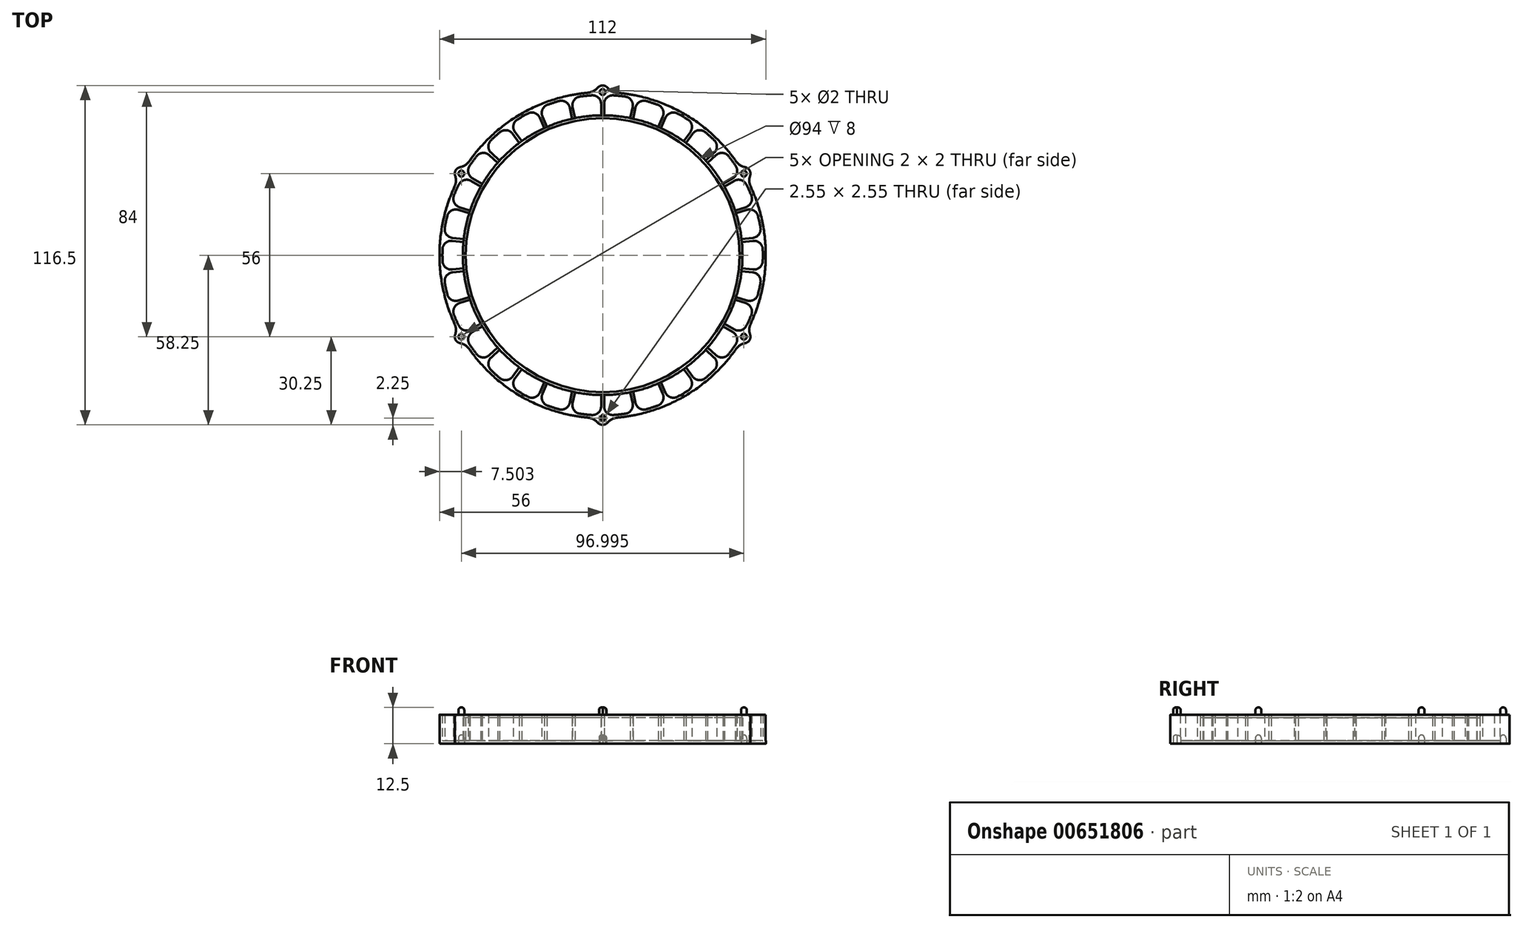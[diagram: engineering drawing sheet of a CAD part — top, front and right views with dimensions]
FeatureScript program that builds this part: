
annotation { "Feature Type Name" : "Feature", "Feature Type Description" : "" }
export const myFeature = defineFeature(function(context is Context, id is Id, definition is map)
    precondition{}
    {
        {
            var Q0;
            Q0=qCreatedBy(makeId("Top.planeOp"),FACE);
            var sketch = newSketch(context, id + "F0", { "sketchPlane" : qUnion([Q0])});
            skCircle(sketch, "E0", {"center": v(0, 0) * mm, "radius": 55 * mm});
            skCircle(sketch, "E1", {"center": v(0, 0) * mm, "radius": 56 * mm});
            skLineSegment(sketch, "E2", {"start": v(0, 60.2) * mm, "end": v(0, -62.26) * mm, "construction": true});
            skLineSegment(sketch, "E3", {"start": v(-62.84, 0) * mm, "end": v(64.36, 0) * mm, "construction": true});
            skLineSegment(sketch, "E4", {"start": v(55, 0) * mm, "end": v(56, 0) * mm});
            skCircle(sketch, "E5", {"center": v(0, 0) * mm, "radius": 48 * mm});
            skCircle(sketch, "E6", {"center": v(0, 0) * mm, "radius": 47 * mm});
            skLineSegment(sketch, "E7.left", {"start": v(-56, 0.5) * mm, "end": v(-56, -0.5) * mm});
            skLineSegment(sketch, "E7.right", {"start": v(56, 0.5) * mm, "end": v(56, -0.5) * mm});
            skLineSegment(sketch, "E8.bottom", {"start": v(0.5, -56) * mm, "end": v(-0.5, -56) * mm});
            skLineSegment(sketch, "E8.top", {"start": v(0.5, 56) * mm, "end": v(-0.5, 56) * mm});
            skLineSegment(sketch, "E8.left", {"start": v(0.5, -56) * mm, "end": v(0.5, 56) * mm});
            skLineSegment(sketch, "E8.right", {"start": v(-0.5, -56) * mm, "end": v(-0.5, 56) * mm});
            skLineSegment(sketch, "E9.bottom", {"start": v(12.13, 54.67) * mm, "end": v(-11.15, -54.88) * mm});
            skLineSegment(sketch, "E9.top", {"start": v(11.15, 54.88) * mm, "end": v(-12.13, -54.67) * mm});
            skLineSegment(sketch, "E9.left", {"start": v(12.13, 54.67) * mm, "end": v(11.15, 54.88) * mm});
            skLineSegment(sketch, "E9.right", {"start": v(-11.15, -54.88) * mm, "end": v(-12.13, -54.67) * mm});
            skLineSegment(sketch, "E10.bottom", {"start": v(-22.32, -51.36) * mm, "end": v(-23.23, -50.95) * mm});
            skLineSegment(sketch, "E10.top", {"start": v(23.23, 50.95) * mm, "end": v(22.32, 51.36) * mm});
            skLineSegment(sketch, "E10.left", {"start": v(-22.32, -51.36) * mm, "end": v(23.23, 50.95) * mm});
            skLineSegment(sketch, "E10.right", {"start": v(-23.23, -50.95) * mm, "end": v(22.32, 51.36) * mm});
            skLineSegment(sketch, "E11.bottom", {"start": v(32.51, 45.6) * mm, "end": v(33.32, 45) * mm});
            skLineSegment(sketch, "E11.top", {"start": v(-33.32, -45) * mm, "end": v(-32.51, -45.6) * mm});
            skLineSegment(sketch, "E11.left", {"start": v(32.51, 45.6) * mm, "end": v(-33.32, -45) * mm});
            skLineSegment(sketch, "E11.right", {"start": v(33.32, 45) * mm, "end": v(-32.51, -45.6) * mm});
            skLineSegment(sketch, "E12.bottom", {"start": v(-41.28, -37.84) * mm, "end": v(-41.95, -37.1) * mm});
            skLineSegment(sketch, "E12.top", {"start": v(41.95, 37.1) * mm, "end": v(41.28, 37.84) * mm});
            skLineSegment(sketch, "E12.left", {"start": v(-41.28, -37.84) * mm, "end": v(41.95, 37.1) * mm});
            skLineSegment(sketch, "E12.right", {"start": v(-41.95, -37.1) * mm, "end": v(41.28, 37.84) * mm});
            skLineSegment(sketch, "E13.bottom", {"start": v(48.25, 28.43) * mm, "end": v(48.75, 27.57) * mm});
            skLineSegment(sketch, "E13.top", {"start": v(-48.75, -27.57) * mm, "end": v(-48.25, -28.43) * mm});
            skLineSegment(sketch, "E13.left", {"start": v(48.25, 28.43) * mm, "end": v(-48.75, -27.57) * mm});
            skLineSegment(sketch, "E13.right", {"start": v(48.75, 27.57) * mm, "end": v(-48.25, -28.43) * mm});
            skLineSegment(sketch, "E14.bottom", {"start": v(-53.1, -17.78) * mm, "end": v(-53.41, -16.83) * mm});
            skLineSegment(sketch, "E14.top", {"start": v(53.41, 16.83) * mm, "end": v(53.1, 17.78) * mm});
            skLineSegment(sketch, "E14.left", {"start": v(-53.1, -17.78) * mm, "end": v(53.41, 16.83) * mm});
            skLineSegment(sketch, "E14.right", {"start": v(-53.41, -16.83) * mm, "end": v(53.1, 17.78) * mm});
            skLineSegment(sketch, "E15.bottom", {"start": v(55.64, 6.35) * mm, "end": v(55.74, 5.36) * mm});
            skLineSegment(sketch, "E15.top", {"start": v(-55.74, -5.36) * mm, "end": v(-55.64, -6.35) * mm});
            skLineSegment(sketch, "E15.left", {"start": v(55.64, 6.35) * mm, "end": v(-55.74, -5.36) * mm});
            skLineSegment(sketch, "E15.right", {"start": v(55.74, 5.36) * mm, "end": v(-55.64, -6.35) * mm});
            skLineSegment(sketch, "E16.bottom", {"start": v(-55.74, 5.36) * mm, "end": v(-55.64, 6.35) * mm});
            skLineSegment(sketch, "E16.top", {"start": v(55.64, -6.35) * mm, "end": v(55.74, -5.36) * mm});
            skLineSegment(sketch, "E16.left", {"start": v(-55.74, 5.36) * mm, "end": v(55.64, -6.35) * mm});
            skLineSegment(sketch, "E16.right", {"start": v(-55.64, 6.35) * mm, "end": v(55.74, -5.36) * mm});
            skLineSegment(sketch, "E17.bottom", {"start": v(53.41, -16.83) * mm, "end": v(53.1, -17.78) * mm});
            skLineSegment(sketch, "E17.top", {"start": v(-53.1, 17.78) * mm, "end": v(-53.41, 16.83) * mm});
            skLineSegment(sketch, "E17.left", {"start": v(53.41, -16.83) * mm, "end": v(-53.1, 17.78) * mm});
            skLineSegment(sketch, "E17.right", {"start": v(53.1, -17.78) * mm, "end": v(-53.41, 16.83) * mm});
            skLineSegment(sketch, "E18.bottom", {"start": v(48.75, -27.57) * mm, "end": v(48.25, -28.43) * mm});
            skLineSegment(sketch, "E18.top", {"start": v(-48.25, 28.43) * mm, "end": v(-48.75, 27.57) * mm});
            skLineSegment(sketch, "E18.left", {"start": v(48.75, -27.57) * mm, "end": v(-48.25, 28.43) * mm});
            skLineSegment(sketch, "E18.right", {"start": v(48.25, -28.43) * mm, "end": v(-48.75, 27.57) * mm});
            skLineSegment(sketch, "E19.bottom", {"start": v(-41.95, 37.1) * mm, "end": v(-41.28, 37.84) * mm});
            skLineSegment(sketch, "E19.top", {"start": v(41.28, -37.84) * mm, "end": v(41.95, -37.1) * mm});
            skLineSegment(sketch, "E19.left", {"start": v(-41.95, 37.1) * mm, "end": v(41.28, -37.84) * mm});
            skLineSegment(sketch, "E19.right", {"start": v(-41.28, 37.84) * mm, "end": v(41.95, -37.1) * mm});
            skLineSegment(sketch, "E20.bottom", {"start": v(-33.32, 45) * mm, "end": v(-32.51, 45.6) * mm});
            skLineSegment(sketch, "E20.top", {"start": v(32.51, -45.6) * mm, "end": v(33.32, -45) * mm});
            skLineSegment(sketch, "E20.left", {"start": v(-33.32, 45) * mm, "end": v(32.51, -45.6) * mm});
            skLineSegment(sketch, "E20.right", {"start": v(-32.51, 45.6) * mm, "end": v(33.32, -45) * mm});
            skLineSegment(sketch, "E21.bottom", {"start": v(-23.23, 50.95) * mm, "end": v(-22.32, 51.36) * mm});
            skLineSegment(sketch, "E21.top", {"start": v(22.32, -51.36) * mm, "end": v(23.23, -50.95) * mm});
            skLineSegment(sketch, "E21.left", {"start": v(-23.23, 50.95) * mm, "end": v(22.32, -51.36) * mm});
            skLineSegment(sketch, "E21.right", {"start": v(-22.32, 51.36) * mm, "end": v(23.23, -50.95) * mm});
            skLineSegment(sketch, "E22.bottom", {"start": v(-12.13, 54.67) * mm, "end": v(-11.15, 54.88) * mm});
            skLineSegment(sketch, "E22.top", {"start": v(11.15, -54.88) * mm, "end": v(12.13, -54.67) * mm});
            skLineSegment(sketch, "E22.left", {"start": v(-12.13, 54.67) * mm, "end": v(11.15, -54.88) * mm});
            skLineSegment(sketch, "E22.right", {"start": v(-11.15, 54.88) * mm, "end": v(12.13, -54.67) * mm});
            skSolve(sketch);
        }
        {
            var Q0;
            {var subQ0=sQuery(id+"F0.wireOp",EDGE,"E7.left");Q0=makeQuery(id+"F0.imprint","IMPRINT",FACE,{"disambiguationData":[TD([[makeQuery(id+"F0.imprint","IMPRINT",EDGE,{"derivedFrom":subQ0}),1.0]])]});}
            var Q1;
            {var subQ5=sQuery(id+"F0.wireOp",EDGE,"E8.top");Q1=makeQuery(id+"F0.imprint","IMPRINT",FACE,{"disambiguationData":[TD([[makeQuery(id+"F0.imprint","IMPRINT",EDGE,{"derivedFrom":subQ5}),1.0]])]});}
            var Q2;
            {var subQ0=sQuery(id+"F0.wireOp",EDGE,"E9.top");var subQ1=sQuery(id+"F0.wireOp",EDGE,"E0");var subQ2=makeQuery(id+"F0.imprint","INTERSECT",VERTEX,{"disambiguationData":[OD(0.0)],"derivedFrom":[subQ1,subQ0]});Q2=makeQuery(id+"F0.imprint","IMPRINT",FACE,{"disambiguationData":[TD([[makeQuery(id+"F0.imprint","IMPRINT",EDGE,{"disambiguationData":[TD([[subQ2,-1.0]])],"derivedFrom":subQ1}),-1.0]])]});}
            var Q3;
            {var subQ5=sQuery(id+"F0.wireOp",EDGE,"E9.left");Q3=makeQuery(id+"F0.imprint","IMPRINT",FACE,{"disambiguationData":[TD([[makeQuery(id+"F0.imprint","IMPRINT",EDGE,{"derivedFrom":subQ5}),1.0]])]});}
            var Q4;
            {var subQ0=sQuery(id+"F0.wireOp",EDGE,"E10.right");var subQ1=sQuery(id+"F0.wireOp",EDGE,"E0");var subQ2=makeQuery(id+"F0.imprint","INTERSECT",VERTEX,{"disambiguationData":[OD(0.0)],"derivedFrom":[subQ1,subQ0]});Q4=makeQuery(id+"F0.imprint","IMPRINT",FACE,{"disambiguationData":[TD([[makeQuery(id+"F0.imprint","IMPRINT",EDGE,{"disambiguationData":[TD([[subQ2,-1.0]])],"derivedFrom":subQ1}),-1.0]])]});}
            var Q5;
            {var subQ5=sQuery(id+"F0.wireOp",EDGE,"E10.top");Q5=makeQuery(id+"F0.imprint","IMPRINT",FACE,{"disambiguationData":[TD([[makeQuery(id+"F0.imprint","IMPRINT",EDGE,{"derivedFrom":subQ5}),1.0]])]});}
            var Q6;
            {var subQ0=sQuery(id+"F0.wireOp",EDGE,"E11.left");var subQ1=sQuery(id+"F0.wireOp",EDGE,"E0");var subQ2=makeQuery(id+"F0.imprint","INTERSECT",VERTEX,{"disambiguationData":[OD(0.0)],"derivedFrom":[subQ1,subQ0]});Q6=makeQuery(id+"F0.imprint","IMPRINT",FACE,{"disambiguationData":[TD([[makeQuery(id+"F0.imprint","IMPRINT",EDGE,{"disambiguationData":[TD([[subQ2,-1.0]])],"derivedFrom":subQ1}),-1.0]])]});}
            var Q7;
            {var subQ3=sQuery(id+"F0.wireOp",EDGE,"E4");var subQ7=sQuery(id+"F0.wireOp",EDGE,"E0");var subQ8=makeQuery(id+"F0.imprint","INTERSECT",VERTEX,{"derivedFrom":[subQ7,subQ3]});Q7=makeQuery(id+"F0.imprint","IMPRINT",FACE,{"disambiguationData":[TD([[makeQuery(id+"F0.imprint","IMPRINT",EDGE,{"disambiguationData":[TD([[subQ8,-1.0]])],"derivedFrom":subQ7}),-1.0]])]});}
            var Q8;
            {var subQ5=sQuery(id+"F0.wireOp",EDGE,"E11.bottom");Q8=makeQuery(id+"F0.imprint","IMPRINT",FACE,{"disambiguationData":[TD([[makeQuery(id+"F0.imprint","IMPRINT",EDGE,{"derivedFrom":subQ5}),-1.0]])]});}
            var Q9;
            {var subQ3=sQuery(id+"F0.wireOp",EDGE,"E4");var subQ5=sQuery(id+"F0.wireOp",EDGE,"E0");var subQ6=makeQuery(id+"F0.imprint","INTERSECT",VERTEX,{"derivedFrom":[subQ5,subQ3]});Q9=makeQuery(id+"F0.imprint","IMPRINT",FACE,{"disambiguationData":[TD([[makeQuery(id+"F0.imprint","IMPRINT",EDGE,{"disambiguationData":[TD([[subQ6,1.0]])],"derivedFrom":subQ5}),-1.0]])]});}
            var Q10;
            {var subQ5=sQuery(id+"F0.wireOp",EDGE,"E8.bottom");Q10=makeQuery(id+"F0.imprint","IMPRINT",FACE,{"disambiguationData":[TD([[makeQuery(id+"F0.imprint","IMPRINT",EDGE,{"derivedFrom":subQ5}),-1.0]])]});}
            var Q11;
            {var subQ0=sQuery(id+"F0.wireOp",EDGE,"E11.right");var subQ1=sQuery(id+"F0.wireOp",EDGE,"E0");var subQ2=makeQuery(id+"F0.imprint","INTERSECT",VERTEX,{"disambiguationData":[OD(1.0)],"derivedFrom":[subQ1,subQ0]});Q11=makeQuery(id+"F0.imprint","IMPRINT",FACE,{"disambiguationData":[TD([[makeQuery(id+"F0.imprint","IMPRINT",EDGE,{"disambiguationData":[TD([[subQ2,-1.0]])],"derivedFrom":subQ1}),-1.0]])]});}
            var Q12;
            {var subQ5=sQuery(id+"F0.wireOp",EDGE,"E11.top");Q12=makeQuery(id+"F0.imprint","IMPRINT",FACE,{"disambiguationData":[TD([[makeQuery(id+"F0.imprint","IMPRINT",EDGE,{"derivedFrom":subQ5}),1.0]])]});}
            var Q13;
            {var subQ5=sQuery(id+"F0.wireOp",EDGE,"E10.bottom");Q13=makeQuery(id+"F0.imprint","IMPRINT",FACE,{"disambiguationData":[TD([[makeQuery(id+"F0.imprint","IMPRINT",EDGE,{"derivedFrom":subQ5}),-1.0]])]});}
            var Q14;
            {var subQ0=sQuery(id+"F0.wireOp",EDGE,"E10.left");var subQ1=sQuery(id+"F0.wireOp",EDGE,"E0");var subQ2=makeQuery(id+"F0.imprint","INTERSECT",VERTEX,{"disambiguationData":[OD(1.0)],"derivedFrom":[subQ1,subQ0]});Q14=makeQuery(id+"F0.imprint","IMPRINT",FACE,{"disambiguationData":[TD([[makeQuery(id+"F0.imprint","IMPRINT",EDGE,{"disambiguationData":[TD([[subQ2,-1.0]])],"derivedFrom":subQ1}),-1.0]])]});}
            var Q15;
            {var subQ5=sQuery(id+"F0.wireOp",EDGE,"E9.right");Q15=makeQuery(id+"F0.imprint","IMPRINT",FACE,{"disambiguationData":[TD([[makeQuery(id+"F0.imprint","IMPRINT",EDGE,{"derivedFrom":subQ5}),-1.0]])]});}
            var Q16;
            {var subQ0=sQuery(id+"F0.wireOp",EDGE,"E9.bottom");var subQ1=sQuery(id+"F0.wireOp",EDGE,"E0");var subQ2=makeQuery(id+"F0.imprint","INTERSECT",VERTEX,{"disambiguationData":[OD(1.0)],"derivedFrom":[subQ1,subQ0]});Q16=makeQuery(id+"F0.imprint","IMPRINT",FACE,{"disambiguationData":[TD([[makeQuery(id+"F0.imprint","IMPRINT",EDGE,{"disambiguationData":[TD([[subQ2,-1.0]])],"derivedFrom":subQ1}),-1.0]])]});}
            var Q17;
            {var subQ0=sQuery(id+"F0.wireOp",EDGE,"E8.left");var subQ1=sQuery(id+"F0.wireOp",EDGE,"E0");var subQ2=makeQuery(id+"F0.imprint","INTERSECT",VERTEX,{"disambiguationData":[OD(0.0)],"derivedFrom":[subQ1,subQ0]});Q17=makeQuery(id+"F0.imprint","IMPRINT",FACE,{"disambiguationData":[TD([[makeQuery(id+"F0.imprint","IMPRINT",EDGE,{"disambiguationData":[TD([[subQ2,-1.0]])],"derivedFrom":subQ1}),1.0]])]});}
            var Q18;
            {var subQ0=sQuery(id+"F0.wireOp",EDGE,"E9.bottom");var subQ1=sQuery(id+"F0.wireOp",EDGE,"E0");var subQ2=makeQuery(id+"F0.imprint","INTERSECT",VERTEX,{"disambiguationData":[OD(0.0)],"derivedFrom":[subQ1,subQ0]});Q18=makeQuery(id+"F0.imprint","IMPRINT",FACE,{"disambiguationData":[TD([[makeQuery(id+"F0.imprint","IMPRINT",EDGE,{"disambiguationData":[TD([[subQ2,-1.0]])],"derivedFrom":subQ1}),1.0]])]});}
            var Q19;
            {var subQ0=sQuery(id+"F0.wireOp",EDGE,"E10.left");var subQ1=sQuery(id+"F0.wireOp",EDGE,"E0");var subQ2=makeQuery(id+"F0.imprint","INTERSECT",VERTEX,{"disambiguationData":[OD(0.0)],"derivedFrom":[subQ1,subQ0]});Q19=makeQuery(id+"F0.imprint","IMPRINT",FACE,{"disambiguationData":[TD([[makeQuery(id+"F0.imprint","IMPRINT",EDGE,{"disambiguationData":[TD([[subQ2,-1.0]])],"derivedFrom":subQ1}),1.0]])]});}
            var Q20;
            {var subQ0=sQuery(id+"F0.wireOp",EDGE,"E11.right");var subQ1=sQuery(id+"F0.wireOp",EDGE,"E0");var subQ2=makeQuery(id+"F0.imprint","INTERSECT",VERTEX,{"disambiguationData":[OD(0.0)],"derivedFrom":[subQ1,subQ0]});Q20=makeQuery(id+"F0.imprint","IMPRINT",FACE,{"disambiguationData":[TD([[makeQuery(id+"F0.imprint","IMPRINT",EDGE,{"disambiguationData":[TD([[subQ2,-1.0]])],"derivedFrom":subQ1}),1.0]])]});}
            var Q21;
            {var subQ0=sQuery(id+"F0.wireOp",EDGE,"E8.right");var subQ1=sQuery(id+"F0.wireOp",EDGE,"E0");var subQ2=makeQuery(id+"F0.imprint","INTERSECT",VERTEX,{"disambiguationData":[OD(1.0)],"derivedFrom":[subQ1,subQ0]});Q21=makeQuery(id+"F0.imprint","IMPRINT",FACE,{"disambiguationData":[TD([[makeQuery(id+"F0.imprint","IMPRINT",EDGE,{"disambiguationData":[TD([[subQ2,-1.0]])],"derivedFrom":subQ1}),1.0]])]});}
            var Q22;
            {var subQ0=sQuery(id+"F0.wireOp",EDGE,"E11.left");var subQ1=sQuery(id+"F0.wireOp",EDGE,"E0");var subQ2=makeQuery(id+"F0.imprint","INTERSECT",VERTEX,{"disambiguationData":[OD(1.0)],"derivedFrom":[subQ1,subQ0]});Q22=makeQuery(id+"F0.imprint","IMPRINT",FACE,{"disambiguationData":[TD([[makeQuery(id+"F0.imprint","IMPRINT",EDGE,{"disambiguationData":[TD([[subQ2,-1.0]])],"derivedFrom":subQ1}),1.0]])]});}
            var Q23;
            {var subQ0=sQuery(id+"F0.wireOp",EDGE,"E10.right");var subQ1=sQuery(id+"F0.wireOp",EDGE,"E0");var subQ2=makeQuery(id+"F0.imprint","INTERSECT",VERTEX,{"disambiguationData":[OD(1.0)],"derivedFrom":[subQ1,subQ0]});Q23=makeQuery(id+"F0.imprint","IMPRINT",FACE,{"disambiguationData":[TD([[makeQuery(id+"F0.imprint","IMPRINT",EDGE,{"disambiguationData":[TD([[subQ2,-1.0]])],"derivedFrom":subQ1}),1.0]])]});}
            var Q24;
            {var subQ0=sQuery(id+"F0.wireOp",EDGE,"E9.top");var subQ1=sQuery(id+"F0.wireOp",EDGE,"E0");var subQ2=makeQuery(id+"F0.imprint","INTERSECT",VERTEX,{"disambiguationData":[OD(1.0)],"derivedFrom":[subQ1,subQ0]});Q24=makeQuery(id+"F0.imprint","IMPRINT",FACE,{"disambiguationData":[TD([[makeQuery(id+"F0.imprint","IMPRINT",EDGE,{"disambiguationData":[TD([[subQ2,-1.0]])],"derivedFrom":subQ1}),1.0]])]});}
            var Q25;
            {var subQ0=sQuery(id+"F0.wireOp",EDGE,"E12.left");var subQ1=sQuery(id+"F0.wireOp",EDGE,"E0");var subQ2=makeQuery(id+"F0.imprint","INTERSECT",VERTEX,{"disambiguationData":[OD(1.0)],"derivedFrom":[subQ1,subQ0]});Q25=makeQuery(id+"F0.imprint","IMPRINT",FACE,{"disambiguationData":[TD([[makeQuery(id+"F0.imprint","IMPRINT",EDGE,{"disambiguationData":[TD([[subQ2,-1.0]])],"derivedFrom":subQ1}),-1.0]])]});}
            var Q26;
            {var subQ5=sQuery(id+"F0.wireOp",EDGE,"E12.bottom");Q26=makeQuery(id+"F0.imprint","IMPRINT",FACE,{"disambiguationData":[TD([[makeQuery(id+"F0.imprint","IMPRINT",EDGE,{"derivedFrom":subQ5}),-1.0]])]});}
            var Q27;
            {var subQ0=sQuery(id+"F0.wireOp",EDGE,"E13.right");var subQ1=sQuery(id+"F0.wireOp",EDGE,"E0");var subQ2=makeQuery(id+"F0.imprint","INTERSECT",VERTEX,{"disambiguationData":[OD(1.0)],"derivedFrom":[subQ1,subQ0]});Q27=makeQuery(id+"F0.imprint","IMPRINT",FACE,{"disambiguationData":[TD([[makeQuery(id+"F0.imprint","IMPRINT",EDGE,{"disambiguationData":[TD([[subQ2,-1.0]])],"derivedFrom":subQ1}),-1.0]])]});}
            var Q28;
            {var subQ5=sQuery(id+"F0.wireOp",EDGE,"E13.top");Q28=makeQuery(id+"F0.imprint","IMPRINT",FACE,{"disambiguationData":[TD([[makeQuery(id+"F0.imprint","IMPRINT",EDGE,{"derivedFrom":subQ5}),1.0]])]});}
            var Q29;
            {var subQ0=sQuery(id+"F0.wireOp",EDGE,"E14.left");var subQ1=sQuery(id+"F0.wireOp",EDGE,"E0");var subQ2=makeQuery(id+"F0.imprint","INTERSECT",VERTEX,{"disambiguationData":[OD(1.0)],"derivedFrom":[subQ1,subQ0]});Q29=makeQuery(id+"F0.imprint","IMPRINT",FACE,{"disambiguationData":[TD([[makeQuery(id+"F0.imprint","IMPRINT",EDGE,{"disambiguationData":[TD([[subQ2,-1.0]])],"derivedFrom":subQ1}),-1.0]])]});}
            var Q30;
            {var subQ0=sQuery(id+"F0.wireOp",EDGE,"E8.left");var subQ1=sQuery(id+"F0.wireOp",EDGE,"E0");var subQ2=makeQuery(id+"F0.imprint","INTERSECT",VERTEX,{"disambiguationData":[OD(1.0)],"derivedFrom":[subQ1,subQ0]});Q30=makeQuery(id+"F0.imprint","IMPRINT",FACE,{"disambiguationData":[TD([[makeQuery(id+"F0.imprint","IMPRINT",EDGE,{"disambiguationData":[TD([[subQ2,-1.0]])],"derivedFrom":subQ1}),-1.0]])]});}
            var Q31;
            {var subQ0=sQuery(id+"F0.wireOp",EDGE,"E22.right");var subQ1=sQuery(id+"F0.wireOp",EDGE,"E0");var subQ2=makeQuery(id+"F0.imprint","INTERSECT",VERTEX,{"disambiguationData":[OD(1.0)],"derivedFrom":[subQ1,subQ0]});Q31=makeQuery(id+"F0.imprint","IMPRINT",FACE,{"disambiguationData":[TD([[makeQuery(id+"F0.imprint","IMPRINT",EDGE,{"disambiguationData":[TD([[subQ2,-1.0]])],"derivedFrom":subQ1}),-1.0]])]});}
            var Q32;
            {var subQ0=sQuery(id+"F0.wireOp",EDGE,"E21.right");var subQ1=sQuery(id+"F0.wireOp",EDGE,"E0");var subQ2=makeQuery(id+"F0.imprint","INTERSECT",VERTEX,{"disambiguationData":[OD(1.0)],"derivedFrom":[subQ1,subQ0]});Q32=makeQuery(id+"F0.imprint","IMPRINT",FACE,{"disambiguationData":[TD([[makeQuery(id+"F0.imprint","IMPRINT",EDGE,{"disambiguationData":[TD([[subQ2,-1.0]])],"derivedFrom":subQ1}),-1.0]])]});}
            var Q33;
            {var subQ0=sQuery(id+"F0.wireOp",EDGE,"E20.right");var subQ1=sQuery(id+"F0.wireOp",EDGE,"E0");var subQ2=makeQuery(id+"F0.imprint","INTERSECT",VERTEX,{"disambiguationData":[OD(1.0)],"derivedFrom":[subQ1,subQ0]});Q33=makeQuery(id+"F0.imprint","IMPRINT",FACE,{"disambiguationData":[TD([[makeQuery(id+"F0.imprint","IMPRINT",EDGE,{"disambiguationData":[TD([[subQ2,-1.0]])],"derivedFrom":subQ1}),-1.0]])]});}
            var Q34;
            {var subQ0=sQuery(id+"F0.wireOp",EDGE,"E19.right");var subQ1=sQuery(id+"F0.wireOp",EDGE,"E0");var subQ2=makeQuery(id+"F0.imprint","INTERSECT",VERTEX,{"disambiguationData":[OD(1.0)],"derivedFrom":[subQ1,subQ0]});Q34=makeQuery(id+"F0.imprint","IMPRINT",FACE,{"disambiguationData":[TD([[makeQuery(id+"F0.imprint","IMPRINT",EDGE,{"disambiguationData":[TD([[subQ2,-1.0]])],"derivedFrom":subQ1}),-1.0]])]});}
            var Q35;
            {var subQ0=sQuery(id+"F0.wireOp",EDGE,"E18.left");var subQ1=sQuery(id+"F0.wireOp",EDGE,"E0");var subQ2=makeQuery(id+"F0.imprint","INTERSECT",VERTEX,{"disambiguationData":[OD(1.0)],"derivedFrom":[subQ1,subQ0]});Q35=makeQuery(id+"F0.imprint","IMPRINT",FACE,{"disambiguationData":[TD([[makeQuery(id+"F0.imprint","IMPRINT",EDGE,{"disambiguationData":[TD([[subQ2,-1.0]])],"derivedFrom":subQ1}),-1.0]])]});}
            var Q36;
            {var subQ0=sQuery(id+"F0.wireOp",EDGE,"E17.left");var subQ1=sQuery(id+"F0.wireOp",EDGE,"E0");var subQ2=makeQuery(id+"F0.imprint","INTERSECT",VERTEX,{"disambiguationData":[OD(1.0)],"derivedFrom":[subQ1,subQ0]});Q36=makeQuery(id+"F0.imprint","IMPRINT",FACE,{"disambiguationData":[TD([[makeQuery(id+"F0.imprint","IMPRINT",EDGE,{"disambiguationData":[TD([[subQ2,-1.0]])],"derivedFrom":subQ1}),-1.0]])]});}
            var Q37;
            {var subQ5=sQuery(id+"F0.wireOp",EDGE,"E22.top");Q37=makeQuery(id+"F0.imprint","IMPRINT",FACE,{"disambiguationData":[TD([[makeQuery(id+"F0.imprint","IMPRINT",EDGE,{"derivedFrom":subQ5}),1.0]])]});}
            var Q38;
            {var subQ5=sQuery(id+"F0.wireOp",EDGE,"E21.top");Q38=makeQuery(id+"F0.imprint","IMPRINT",FACE,{"disambiguationData":[TD([[makeQuery(id+"F0.imprint","IMPRINT",EDGE,{"derivedFrom":subQ5}),1.0]])]});}
            var Q39;
            {var subQ5=sQuery(id+"F0.wireOp",EDGE,"E20.top");Q39=makeQuery(id+"F0.imprint","IMPRINT",FACE,{"disambiguationData":[TD([[makeQuery(id+"F0.imprint","IMPRINT",EDGE,{"derivedFrom":subQ5}),1.0]])]});}
            var Q40;
            {var subQ5=sQuery(id+"F0.wireOp",EDGE,"E19.top");Q40=makeQuery(id+"F0.imprint","IMPRINT",FACE,{"disambiguationData":[TD([[makeQuery(id+"F0.imprint","IMPRINT",EDGE,{"derivedFrom":subQ5}),1.0]])]});}
            var Q41;
            {var subQ5=sQuery(id+"F0.wireOp",EDGE,"E18.bottom");Q41=makeQuery(id+"F0.imprint","IMPRINT",FACE,{"disambiguationData":[TD([[makeQuery(id+"F0.imprint","IMPRINT",EDGE,{"derivedFrom":subQ5}),-1.0]])]});}
            var Q42;
            {var subQ5=sQuery(id+"F0.wireOp",EDGE,"E17.bottom");Q42=makeQuery(id+"F0.imprint","IMPRINT",FACE,{"disambiguationData":[TD([[makeQuery(id+"F0.imprint","IMPRINT",EDGE,{"derivedFrom":subQ5}),-1.0]])]});}
            var Q43;
            {var subQ5=sQuery(id+"F0.wireOp",EDGE,"E16.top");Q43=makeQuery(id+"F0.imprint","IMPRINT",FACE,{"disambiguationData":[TD([[makeQuery(id+"F0.imprint","IMPRINT",EDGE,{"derivedFrom":subQ5}),1.0]])]});}
            var Q44;
            {var subQ5=sQuery(id+"F0.wireOp",EDGE,"E15.bottom");Q44=makeQuery(id+"F0.imprint","IMPRINT",FACE,{"disambiguationData":[TD([[makeQuery(id+"F0.imprint","IMPRINT",EDGE,{"derivedFrom":subQ5}),-1.0]])]});}
            var Q45;
            {var subQ5=sQuery(id+"F0.wireOp",EDGE,"E14.top");Q45=makeQuery(id+"F0.imprint","IMPRINT",FACE,{"disambiguationData":[TD([[makeQuery(id+"F0.imprint","IMPRINT",EDGE,{"derivedFrom":subQ5}),1.0]])]});}
            var Q46;
            {var subQ0=sQuery(id+"F0.wireOp",EDGE,"E14.right");var subQ1=sQuery(id+"F0.wireOp",EDGE,"E0");var subQ2=makeQuery(id+"F0.imprint","INTERSECT",VERTEX,{"disambiguationData":[OD(0.0)],"derivedFrom":[subQ1,subQ0]});Q46=makeQuery(id+"F0.imprint","IMPRINT",FACE,{"disambiguationData":[TD([[makeQuery(id+"F0.imprint","IMPRINT",EDGE,{"disambiguationData":[TD([[subQ2,-1.0]])],"derivedFrom":subQ1}),-1.0]])]});}
            var Q47;
            {var subQ0=sQuery(id+"F0.wireOp",EDGE,"E12.right");var subQ1=sQuery(id+"F0.wireOp",EDGE,"E0");var subQ2=makeQuery(id+"F0.imprint","INTERSECT",VERTEX,{"disambiguationData":[OD(0.0)],"derivedFrom":[subQ1,subQ0]});Q47=makeQuery(id+"F0.imprint","IMPRINT",FACE,{"disambiguationData":[TD([[makeQuery(id+"F0.imprint","IMPRINT",EDGE,{"disambiguationData":[TD([[subQ2,-1.0]])],"derivedFrom":subQ1}),-1.0]])]});}
            var Q48;
            {var subQ5=sQuery(id+"F0.wireOp",EDGE,"E12.top");Q48=makeQuery(id+"F0.imprint","IMPRINT",FACE,{"disambiguationData":[TD([[makeQuery(id+"F0.imprint","IMPRINT",EDGE,{"derivedFrom":subQ5}),1.0]])]});}
            var Q49;
            {var subQ0=sQuery(id+"F0.wireOp",EDGE,"E13.left");var subQ1=sQuery(id+"F0.wireOp",EDGE,"E0");var subQ2=makeQuery(id+"F0.imprint","INTERSECT",VERTEX,{"disambiguationData":[OD(0.0)],"derivedFrom":[subQ1,subQ0]});Q49=makeQuery(id+"F0.imprint","IMPRINT",FACE,{"disambiguationData":[TD([[makeQuery(id+"F0.imprint","IMPRINT",EDGE,{"disambiguationData":[TD([[subQ2,-1.0]])],"derivedFrom":subQ1}),-1.0]])]});}
            var Q50;
            {var subQ5=sQuery(id+"F0.wireOp",EDGE,"E13.bottom");Q50=makeQuery(id+"F0.imprint","IMPRINT",FACE,{"disambiguationData":[TD([[makeQuery(id+"F0.imprint","IMPRINT",EDGE,{"derivedFrom":subQ5}),-1.0]])]});}
            var Q51;
            {var subQ0=sQuery(id+"F0.wireOp",EDGE,"E15.left");var subQ1=sQuery(id+"F0.wireOp",EDGE,"E0");var subQ2=makeQuery(id+"F0.imprint","INTERSECT",VERTEX,{"disambiguationData":[OD(0.0)],"derivedFrom":[subQ1,subQ0]});Q51=makeQuery(id+"F0.imprint","IMPRINT",FACE,{"disambiguationData":[TD([[makeQuery(id+"F0.imprint","IMPRINT",EDGE,{"disambiguationData":[TD([[subQ2,-1.0]])],"derivedFrom":subQ1}),-1.0]])]});}
            var Q52;
            {var subQ0=sQuery(id+"F0.wireOp",EDGE,"E16.left");var subQ1=sQuery(id+"F0.wireOp",EDGE,"E0");var subQ2=makeQuery(id+"F0.imprint","INTERSECT",VERTEX,{"disambiguationData":[OD(1.0)],"derivedFrom":[subQ1,subQ0]});Q52=makeQuery(id+"F0.imprint","IMPRINT",FACE,{"disambiguationData":[TD([[makeQuery(id+"F0.imprint","IMPRINT",EDGE,{"disambiguationData":[TD([[subQ2,-1.0]])],"derivedFrom":subQ1}),1.0]])]});}
            var Q53;
            {var subQ0=sQuery(id+"F0.wireOp",EDGE,"E15.right");var subQ1=sQuery(id+"F0.wireOp",EDGE,"E0");var subQ2=makeQuery(id+"F0.imprint","INTERSECT",VERTEX,{"disambiguationData":[OD(0.0)],"derivedFrom":[subQ1,subQ0]});Q53=makeQuery(id+"F0.imprint","IMPRINT",FACE,{"disambiguationData":[TD([[makeQuery(id+"F0.imprint","IMPRINT",EDGE,{"disambiguationData":[TD([[subQ2,-1.0]])],"derivedFrom":subQ1}),1.0]])]});}
            var Q54;
            {var subQ0=sQuery(id+"F0.wireOp",EDGE,"E14.left");var subQ1=sQuery(id+"F0.wireOp",EDGE,"E0");var subQ2=makeQuery(id+"F0.imprint","INTERSECT",VERTEX,{"disambiguationData":[OD(0.0)],"derivedFrom":[subQ1,subQ0]});Q54=makeQuery(id+"F0.imprint","IMPRINT",FACE,{"disambiguationData":[TD([[makeQuery(id+"F0.imprint","IMPRINT",EDGE,{"disambiguationData":[TD([[subQ2,-1.0]])],"derivedFrom":subQ1}),1.0]])]});}
            var Q55;
            {var subQ0=sQuery(id+"F0.wireOp",EDGE,"E13.right");var subQ1=sQuery(id+"F0.wireOp",EDGE,"E0");var subQ2=makeQuery(id+"F0.imprint","INTERSECT",VERTEX,{"disambiguationData":[OD(0.0)],"derivedFrom":[subQ1,subQ0]});Q55=makeQuery(id+"F0.imprint","IMPRINT",FACE,{"disambiguationData":[TD([[makeQuery(id+"F0.imprint","IMPRINT",EDGE,{"disambiguationData":[TD([[subQ2,-1.0]])],"derivedFrom":subQ1}),1.0]])]});}
            var Q56;
            {var subQ0=sQuery(id+"F0.wireOp",EDGE,"E12.left");var subQ1=sQuery(id+"F0.wireOp",EDGE,"E0");var subQ2=makeQuery(id+"F0.imprint","INTERSECT",VERTEX,{"disambiguationData":[OD(0.0)],"derivedFrom":[subQ1,subQ0]});Q56=makeQuery(id+"F0.imprint","IMPRINT",FACE,{"disambiguationData":[TD([[makeQuery(id+"F0.imprint","IMPRINT",EDGE,{"disambiguationData":[TD([[subQ2,-1.0]])],"derivedFrom":subQ1}),1.0]])]});}
            var Q57;
            {var subQ0=sQuery(id+"F0.wireOp",EDGE,"E8.right");var subQ1=sQuery(id+"F0.wireOp",EDGE,"E0");var subQ2=makeQuery(id+"F0.imprint","INTERSECT",VERTEX,{"disambiguationData":[OD(0.0)],"derivedFrom":[subQ1,subQ0]});Q57=makeQuery(id+"F0.imprint","IMPRINT",FACE,{"disambiguationData":[TD([[makeQuery(id+"F0.imprint","IMPRINT",EDGE,{"disambiguationData":[TD([[subQ2,-1.0]])],"derivedFrom":subQ1}),-1.0]])]});}
            var Q58;
            {var subQ5=sQuery(id+"F0.wireOp",EDGE,"E22.bottom");Q58=makeQuery(id+"F0.imprint","IMPRINT",FACE,{"disambiguationData":[TD([[makeQuery(id+"F0.imprint","IMPRINT",EDGE,{"derivedFrom":subQ5}),-1.0]])]});}
            var Q59;
            {var subQ5=sQuery(id+"F0.wireOp",EDGE,"E21.bottom");Q59=makeQuery(id+"F0.imprint","IMPRINT",FACE,{"disambiguationData":[TD([[makeQuery(id+"F0.imprint","IMPRINT",EDGE,{"derivedFrom":subQ5}),-1.0]])]});}
            var Q60;
            {var subQ0=sQuery(id+"F0.wireOp",EDGE,"E22.left");var subQ1=sQuery(id+"F0.wireOp",EDGE,"E0");var subQ2=makeQuery(id+"F0.imprint","INTERSECT",VERTEX,{"disambiguationData":[OD(0.0)],"derivedFrom":[subQ1,subQ0]});Q60=makeQuery(id+"F0.imprint","IMPRINT",FACE,{"disambiguationData":[TD([[makeQuery(id+"F0.imprint","IMPRINT",EDGE,{"disambiguationData":[TD([[subQ2,-1.0]])],"derivedFrom":subQ1}),-1.0]])]});}
            var Q61;
            {var subQ0=sQuery(id+"F0.wireOp",EDGE,"E21.left");var subQ1=sQuery(id+"F0.wireOp",EDGE,"E0");var subQ2=makeQuery(id+"F0.imprint","INTERSECT",VERTEX,{"disambiguationData":[OD(0.0)],"derivedFrom":[subQ1,subQ0]});Q61=makeQuery(id+"F0.imprint","IMPRINT",FACE,{"disambiguationData":[TD([[makeQuery(id+"F0.imprint","IMPRINT",EDGE,{"disambiguationData":[TD([[subQ2,-1.0]])],"derivedFrom":subQ1}),-1.0]])]});}
            var Q62;
            {var subQ5=sQuery(id+"F0.wireOp",EDGE,"E20.bottom");Q62=makeQuery(id+"F0.imprint","IMPRINT",FACE,{"disambiguationData":[TD([[makeQuery(id+"F0.imprint","IMPRINT",EDGE,{"derivedFrom":subQ5}),-1.0]])]});}
            var Q63;
            {var subQ0=sQuery(id+"F0.wireOp",EDGE,"E20.left");var subQ1=sQuery(id+"F0.wireOp",EDGE,"E0");var subQ2=makeQuery(id+"F0.imprint","INTERSECT",VERTEX,{"disambiguationData":[OD(0.0)],"derivedFrom":[subQ1,subQ0]});Q63=makeQuery(id+"F0.imprint","IMPRINT",FACE,{"disambiguationData":[TD([[makeQuery(id+"F0.imprint","IMPRINT",EDGE,{"disambiguationData":[TD([[subQ2,-1.0]])],"derivedFrom":subQ1}),-1.0]])]});}
            var Q64;
            {var subQ0=sQuery(id+"F0.wireOp",EDGE,"E19.left");var subQ1=sQuery(id+"F0.wireOp",EDGE,"E0");var subQ2=makeQuery(id+"F0.imprint","INTERSECT",VERTEX,{"disambiguationData":[OD(0.0)],"derivedFrom":[subQ1,subQ0]});Q64=makeQuery(id+"F0.imprint","IMPRINT",FACE,{"disambiguationData":[TD([[makeQuery(id+"F0.imprint","IMPRINT",EDGE,{"disambiguationData":[TD([[subQ2,-1.0]])],"derivedFrom":subQ1}),-1.0]])]});}
            var Q65;
            {var subQ5=sQuery(id+"F0.wireOp",EDGE,"E19.bottom");Q65=makeQuery(id+"F0.imprint","IMPRINT",FACE,{"disambiguationData":[TD([[makeQuery(id+"F0.imprint","IMPRINT",EDGE,{"derivedFrom":subQ5}),-1.0]])]});}
            var Q66;
            {var subQ0=sQuery(id+"F0.wireOp",EDGE,"E19.right");var subQ1=sQuery(id+"F0.wireOp",EDGE,"E0");var subQ2=makeQuery(id+"F0.imprint","INTERSECT",VERTEX,{"disambiguationData":[OD(0.0)],"derivedFrom":[subQ1,subQ0]});Q66=makeQuery(id+"F0.imprint","IMPRINT",FACE,{"disambiguationData":[TD([[makeQuery(id+"F0.imprint","IMPRINT",EDGE,{"disambiguationData":[TD([[subQ2,-1.0]])],"derivedFrom":subQ1}),1.0]])]});}
            var Q67;
            {var subQ0=sQuery(id+"F0.wireOp",EDGE,"E20.right");var subQ1=sQuery(id+"F0.wireOp",EDGE,"E0");var subQ2=makeQuery(id+"F0.imprint","INTERSECT",VERTEX,{"disambiguationData":[OD(0.0)],"derivedFrom":[subQ1,subQ0]});Q67=makeQuery(id+"F0.imprint","IMPRINT",FACE,{"disambiguationData":[TD([[makeQuery(id+"F0.imprint","IMPRINT",EDGE,{"disambiguationData":[TD([[subQ2,-1.0]])],"derivedFrom":subQ1}),1.0]])]});}
            var Q68;
            {var subQ0=sQuery(id+"F0.wireOp",EDGE,"E21.right");var subQ1=sQuery(id+"F0.wireOp",EDGE,"E0");var subQ2=makeQuery(id+"F0.imprint","INTERSECT",VERTEX,{"disambiguationData":[OD(0.0)],"derivedFrom":[subQ1,subQ0]});Q68=makeQuery(id+"F0.imprint","IMPRINT",FACE,{"disambiguationData":[TD([[makeQuery(id+"F0.imprint","IMPRINT",EDGE,{"disambiguationData":[TD([[subQ2,-1.0]])],"derivedFrom":subQ1}),1.0]])]});}
            var Q69;
            {var subQ0=sQuery(id+"F0.wireOp",EDGE,"E22.right");var subQ1=sQuery(id+"F0.wireOp",EDGE,"E0");var subQ2=makeQuery(id+"F0.imprint","INTERSECT",VERTEX,{"disambiguationData":[OD(0.0)],"derivedFrom":[subQ1,subQ0]});Q69=makeQuery(id+"F0.imprint","IMPRINT",FACE,{"disambiguationData":[TD([[makeQuery(id+"F0.imprint","IMPRINT",EDGE,{"disambiguationData":[TD([[subQ2,-1.0]])],"derivedFrom":subQ1}),1.0]])]});}
            var Q70;
            {var subQ5=sQuery(id+"F0.wireOp",EDGE,"E16.bottom");Q70=makeQuery(id+"F0.imprint","IMPRINT",FACE,{"disambiguationData":[TD([[makeQuery(id+"F0.imprint","IMPRINT",EDGE,{"derivedFrom":subQ5}),-1.0]])]});}
            var Q71;
            {var subQ5=sQuery(id+"F0.wireOp",EDGE,"E18.top");Q71=makeQuery(id+"F0.imprint","IMPRINT",FACE,{"disambiguationData":[TD([[makeQuery(id+"F0.imprint","IMPRINT",EDGE,{"derivedFrom":subQ5}),1.0]])]});}
            var Q72;
            {var subQ0=sQuery(id+"F0.wireOp",EDGE,"E18.right");var subQ1=sQuery(id+"F0.wireOp",EDGE,"E0");var subQ2=makeQuery(id+"F0.imprint","INTERSECT",VERTEX,{"disambiguationData":[OD(0.0)],"derivedFrom":[subQ1,subQ0]});Q72=makeQuery(id+"F0.imprint","IMPRINT",FACE,{"disambiguationData":[TD([[makeQuery(id+"F0.imprint","IMPRINT",EDGE,{"disambiguationData":[TD([[subQ2,-1.0]])],"derivedFrom":subQ1}),-1.0]])]});}
            var Q73;
            {var subQ5=sQuery(id+"F0.wireOp",EDGE,"E17.top");Q73=makeQuery(id+"F0.imprint","IMPRINT",FACE,{"disambiguationData":[TD([[makeQuery(id+"F0.imprint","IMPRINT",EDGE,{"derivedFrom":subQ5}),1.0]])]});}
            var Q74;
            {var subQ0=sQuery(id+"F0.wireOp",EDGE,"E17.right");var subQ1=sQuery(id+"F0.wireOp",EDGE,"E0");var subQ2=makeQuery(id+"F0.imprint","INTERSECT",VERTEX,{"disambiguationData":[OD(0.0)],"derivedFrom":[subQ1,subQ0]});Q74=makeQuery(id+"F0.imprint","IMPRINT",FACE,{"disambiguationData":[TD([[makeQuery(id+"F0.imprint","IMPRINT",EDGE,{"disambiguationData":[TD([[subQ2,-1.0]])],"derivedFrom":subQ1}),-1.0]])]});}
            var Q75;
            {var subQ0=sQuery(id+"F0.wireOp",EDGE,"E18.left");var subQ1=sQuery(id+"F0.wireOp",EDGE,"E0");var subQ2=makeQuery(id+"F0.imprint","INTERSECT",VERTEX,{"disambiguationData":[OD(0.0)],"derivedFrom":[subQ1,subQ0]});Q75=makeQuery(id+"F0.imprint","IMPRINT",FACE,{"disambiguationData":[TD([[makeQuery(id+"F0.imprint","IMPRINT",EDGE,{"disambiguationData":[TD([[subQ2,-1.0]])],"derivedFrom":subQ1}),1.0]])]});}
            var Q76;
            {var subQ0=sQuery(id+"F0.wireOp",EDGE,"E17.left");var subQ1=sQuery(id+"F0.wireOp",EDGE,"E0");var subQ2=makeQuery(id+"F0.imprint","INTERSECT",VERTEX,{"disambiguationData":[OD(0.0)],"derivedFrom":[subQ1,subQ0]});Q76=makeQuery(id+"F0.imprint","IMPRINT",FACE,{"disambiguationData":[TD([[makeQuery(id+"F0.imprint","IMPRINT",EDGE,{"disambiguationData":[TD([[subQ2,-1.0]])],"derivedFrom":subQ1}),1.0]])]});}
            var Q77;
            {var subQ0=sQuery(id+"F0.wireOp",EDGE,"E16.right");var subQ1=sQuery(id+"F0.wireOp",EDGE,"E0");var subQ2=makeQuery(id+"F0.imprint","INTERSECT",VERTEX,{"disambiguationData":[OD(0.0)],"derivedFrom":[subQ1,subQ0]});Q77=makeQuery(id+"F0.imprint","IMPRINT",FACE,{"disambiguationData":[TD([[makeQuery(id+"F0.imprint","IMPRINT",EDGE,{"disambiguationData":[TD([[subQ2,-1.0]])],"derivedFrom":subQ1}),1.0]])]});}
            var Q78;
            {var subQ5=sQuery(id+"F0.wireOp",EDGE,"E15.top");Q78=makeQuery(id+"F0.imprint","IMPRINT",FACE,{"disambiguationData":[TD([[makeQuery(id+"F0.imprint","IMPRINT",EDGE,{"derivedFrom":subQ5}),1.0]])]});}
            var Q79;
            {var subQ0=sQuery(id+"F0.wireOp",EDGE,"E15.left");var subQ1=sQuery(id+"F0.wireOp",EDGE,"E0");var subQ2=makeQuery(id+"F0.imprint","INTERSECT",VERTEX,{"disambiguationData":[OD(1.0)],"derivedFrom":[subQ1,subQ0]});Q79=makeQuery(id+"F0.imprint","IMPRINT",FACE,{"disambiguationData":[TD([[makeQuery(id+"F0.imprint","IMPRINT",EDGE,{"disambiguationData":[TD([[subQ2,-1.0]])],"derivedFrom":subQ1}),1.0]])]});}
            var Q80;
            {var subQ0=sQuery(id+"F0.wireOp",EDGE,"E12.right");var subQ1=sQuery(id+"F0.wireOp",EDGE,"E0");var subQ2=makeQuery(id+"F0.imprint","INTERSECT",VERTEX,{"disambiguationData":[OD(1.0)],"derivedFrom":[subQ1,subQ0]});Q80=makeQuery(id+"F0.imprint","IMPRINT",FACE,{"disambiguationData":[TD([[makeQuery(id+"F0.imprint","IMPRINT",EDGE,{"disambiguationData":[TD([[subQ2,-1.0]])],"derivedFrom":subQ1}),1.0]])]});}
            var Q81;
            {var subQ0=sQuery(id+"F0.wireOp",EDGE,"E13.left");var subQ1=sQuery(id+"F0.wireOp",EDGE,"E0");var subQ2=makeQuery(id+"F0.imprint","INTERSECT",VERTEX,{"disambiguationData":[OD(1.0)],"derivedFrom":[subQ1,subQ0]});Q81=makeQuery(id+"F0.imprint","IMPRINT",FACE,{"disambiguationData":[TD([[makeQuery(id+"F0.imprint","IMPRINT",EDGE,{"disambiguationData":[TD([[subQ2,-1.0]])],"derivedFrom":subQ1}),1.0]])]});}
            var Q82;
            {var subQ5=sQuery(id+"F0.wireOp",EDGE,"E14.bottom");Q82=makeQuery(id+"F0.imprint","IMPRINT",FACE,{"disambiguationData":[TD([[makeQuery(id+"F0.imprint","IMPRINT",EDGE,{"derivedFrom":subQ5}),-1.0]])]});}
            var Q83;
            {var subQ0=sQuery(id+"F0.wireOp",EDGE,"E15.right");var subQ1=sQuery(id+"F0.wireOp",EDGE,"E0");var subQ2=makeQuery(id+"F0.imprint","INTERSECT",VERTEX,{"disambiguationData":[OD(1.0)],"derivedFrom":[subQ1,subQ0]});Q83=makeQuery(id+"F0.imprint","IMPRINT",FACE,{"disambiguationData":[TD([[makeQuery(id+"F0.imprint","IMPRINT",EDGE,{"disambiguationData":[TD([[subQ2,-1.0]])],"derivedFrom":subQ1}),-1.0]])]});}
            var Q84;
            {var subQ0=sQuery(id+"F0.wireOp",EDGE,"E14.right");var subQ1=sQuery(id+"F0.wireOp",EDGE,"E0");var subQ2=makeQuery(id+"F0.imprint","INTERSECT",VERTEX,{"disambiguationData":[OD(1.0)],"derivedFrom":[subQ1,subQ0]});Q84=makeQuery(id+"F0.imprint","IMPRINT",FACE,{"disambiguationData":[TD([[makeQuery(id+"F0.imprint","IMPRINT",EDGE,{"disambiguationData":[TD([[subQ2,-1.0]])],"derivedFrom":subQ1}),1.0]])]});}
            var Q85;
            {var subQ0=sQuery(id+"F0.wireOp",EDGE,"E22.left");var subQ1=sQuery(id+"F0.wireOp",EDGE,"E0");var subQ2=makeQuery(id+"F0.imprint","INTERSECT",VERTEX,{"disambiguationData":[OD(1.0)],"derivedFrom":[subQ1,subQ0]});Q85=makeQuery(id+"F0.imprint","IMPRINT",FACE,{"disambiguationData":[TD([[makeQuery(id+"F0.imprint","IMPRINT",EDGE,{"disambiguationData":[TD([[subQ2,-1.0]])],"derivedFrom":subQ1}),1.0]])]});}
            var Q86;
            {var subQ0=sQuery(id+"F0.wireOp",EDGE,"E21.left");var subQ1=sQuery(id+"F0.wireOp",EDGE,"E0");var subQ2=makeQuery(id+"F0.imprint","INTERSECT",VERTEX,{"disambiguationData":[OD(1.0)],"derivedFrom":[subQ1,subQ0]});Q86=makeQuery(id+"F0.imprint","IMPRINT",FACE,{"disambiguationData":[TD([[makeQuery(id+"F0.imprint","IMPRINT",EDGE,{"disambiguationData":[TD([[subQ2,-1.0]])],"derivedFrom":subQ1}),1.0]])]});}
            var Q87;
            {var subQ0=sQuery(id+"F0.wireOp",EDGE,"E20.left");var subQ1=sQuery(id+"F0.wireOp",EDGE,"E0");var subQ2=makeQuery(id+"F0.imprint","INTERSECT",VERTEX,{"disambiguationData":[OD(1.0)],"derivedFrom":[subQ1,subQ0]});Q87=makeQuery(id+"F0.imprint","IMPRINT",FACE,{"disambiguationData":[TD([[makeQuery(id+"F0.imprint","IMPRINT",EDGE,{"disambiguationData":[TD([[subQ2,-1.0]])],"derivedFrom":subQ1}),1.0]])]});}
            var Q88;
            {var subQ0=sQuery(id+"F0.wireOp",EDGE,"E19.left");var subQ1=sQuery(id+"F0.wireOp",EDGE,"E0");var subQ2=makeQuery(id+"F0.imprint","INTERSECT",VERTEX,{"disambiguationData":[OD(1.0)],"derivedFrom":[subQ1,subQ0]});Q88=makeQuery(id+"F0.imprint","IMPRINT",FACE,{"disambiguationData":[TD([[makeQuery(id+"F0.imprint","IMPRINT",EDGE,{"disambiguationData":[TD([[subQ2,-1.0]])],"derivedFrom":subQ1}),1.0]])]});}
            var Q89;
            {var subQ0=sQuery(id+"F0.wireOp",EDGE,"E18.right");var subQ1=sQuery(id+"F0.wireOp",EDGE,"E0");var subQ2=makeQuery(id+"F0.imprint","INTERSECT",VERTEX,{"disambiguationData":[OD(1.0)],"derivedFrom":[subQ1,subQ0]});Q89=makeQuery(id+"F0.imprint","IMPRINT",FACE,{"disambiguationData":[TD([[makeQuery(id+"F0.imprint","IMPRINT",EDGE,{"disambiguationData":[TD([[subQ2,-1.0]])],"derivedFrom":subQ1}),1.0]])]});}
            var Q90;
            {var subQ0=sQuery(id+"F0.wireOp",EDGE,"E17.right");var subQ1=sQuery(id+"F0.wireOp",EDGE,"E0");var subQ2=makeQuery(id+"F0.imprint","INTERSECT",VERTEX,{"disambiguationData":[OD(1.0)],"derivedFrom":[subQ1,subQ0]});Q90=makeQuery(id+"F0.imprint","IMPRINT",FACE,{"disambiguationData":[TD([[makeQuery(id+"F0.imprint","IMPRINT",EDGE,{"disambiguationData":[TD([[subQ2,-1.0]])],"derivedFrom":subQ1}),1.0]])]});}
            extrude(context, id + "F1", {"entities" : qUnion([Q0, Q1, Q2, Q3, Q4, Q5, Q6, Q7, Q8, Q9, Q10, Q11, Q12, Q13, Q14, Q15, Q16, Q17, Q18, Q19, Q20, Q21, Q22, Q23, Q24, Q25, Q26, Q27, Q28, Q29, Q30, Q31, Q32, Q33, Q34, Q35, Q36, Q37, Q38, Q39, Q40, Q41, Q42, Q43, Q44, Q45, Q46, Q47, Q48, Q49, Q50, Q51, Q52, Q53, Q54, Q55, Q56, Q57, Q58, Q59, Q60, Q61, Q62, Q63, Q64, Q65, Q66, Q67, Q68, Q69, Q70, Q71, Q72, Q73, Q74, Q75, Q76, Q77, Q78, Q79, Q80, Q81, Q82, Q83, Q84, Q85, Q86, Q87, Q88, Q89, Q90]), "depth" : 10 * mm, "offsetDistance" : 25 * mm});
        }
        {
            var Q0;
            Q0=makeQuery(id+"F0.imprint","IMPRINT",FACE,{"disambiguationData":[TD([[makeQuery(id+"F0.imprint","IMPRINT",EDGE,{"derivedFrom":sQuery(id+"F0.wireOp",EDGE,"E5")}),1.0]])]});
            extrude(context, id + "F2", {"entities" : qUnion([Q0]), "depth" : 9 * mm, "offsetDistance" : 25 * mm});
        }
        {
            var Q0;
            {var subQ0=sQuery(id+"F0.wireOp",EDGE,"E11.right");var subQ1=sQuery(id+"F0.wireOp",EDGE,"E0");Q0=makeQuery(id+"F1.opExtrude","SWEPT_EDGE",EDGE,{"disambiguationData":[OSD([subQ1,subQ0]),TDD([makeQuery(id+"F0.imprint","INTERSECT",VERTEX,{"disambiguationData":[OD(0.0)],"derivedFrom":[subQ1,subQ0]})])]});}
            var Q1;
            {var subQ0=sQuery(id+"F0.wireOp",EDGE,"E10.left");var subQ1=sQuery(id+"F0.wireOp",EDGE,"E0");Q1=makeQuery(id+"F1.opExtrude","SWEPT_EDGE",EDGE,{"disambiguationData":[OSD([subQ1,subQ0]),TDD([makeQuery(id+"F0.imprint","INTERSECT",VERTEX,{"disambiguationData":[OD(0.0)],"derivedFrom":[subQ1,subQ0]})])]});}
            var Q2;
            {var subQ0=sQuery(id+"F0.wireOp",EDGE,"E9.bottom");var subQ1=sQuery(id+"F0.wireOp",EDGE,"E0");Q2=makeQuery(id+"F1.opExtrude","SWEPT_EDGE",EDGE,{"disambiguationData":[OSD([subQ1,subQ0]),TDD([makeQuery(id+"F0.imprint","INTERSECT",VERTEX,{"disambiguationData":[OD(0.0)],"derivedFrom":[subQ1,subQ0]})])]});}
            var Q3;
            {var subQ0=sQuery(id+"F0.wireOp",EDGE,"E8.left");var subQ1=sQuery(id+"F0.wireOp",EDGE,"E0");Q3=makeQuery(id+"F1.opExtrude","SWEPT_EDGE",EDGE,{"disambiguationData":[OSD([subQ1,subQ0]),TDD([makeQuery(id+"F0.imprint","INTERSECT",VERTEX,{"disambiguationData":[OD(0.0)],"derivedFrom":[subQ1,subQ0]})])]});}
            var Q4;
            {var subQ0=sQuery(id+"F0.wireOp",EDGE,"E8.right");var subQ1=sQuery(id+"F0.wireOp",EDGE,"E0");Q4=makeQuery(id+"F1.opExtrude","SWEPT_EDGE",EDGE,{"disambiguationData":[OSD([subQ1,subQ0]),TDD([makeQuery(id+"F0.imprint","INTERSECT",VERTEX,{"disambiguationData":[OD(0.0)],"derivedFrom":[subQ1,subQ0]})])]});}
            var Q5;
            {var subQ0=sQuery(id+"F0.wireOp",EDGE,"E9.top");var subQ1=sQuery(id+"F0.wireOp",EDGE,"E0");Q5=makeQuery(id+"F1.opExtrude","SWEPT_EDGE",EDGE,{"disambiguationData":[OSD([subQ1,subQ0]),TDD([makeQuery(id+"F0.imprint","INTERSECT",VERTEX,{"disambiguationData":[OD(0.0)],"derivedFrom":[subQ1,subQ0]})])]});}
            var Q6;
            {var subQ0=sQuery(id+"F0.wireOp",EDGE,"E10.right");var subQ1=sQuery(id+"F0.wireOp",EDGE,"E0");Q6=makeQuery(id+"F1.opExtrude","SWEPT_EDGE",EDGE,{"disambiguationData":[OSD([subQ1,subQ0]),TDD([makeQuery(id+"F0.imprint","INTERSECT",VERTEX,{"disambiguationData":[OD(0.0)],"derivedFrom":[subQ1,subQ0]})])]});}
            var Q7;
            {var subQ0=sQuery(id+"F0.wireOp",EDGE,"E11.left");var subQ1=sQuery(id+"F0.wireOp",EDGE,"E0");Q7=makeQuery(id+"F1.opExtrude","SWEPT_EDGE",EDGE,{"disambiguationData":[OSD([subQ1,subQ0]),TDD([makeQuery(id+"F0.imprint","INTERSECT",VERTEX,{"disambiguationData":[OD(0.0)],"derivedFrom":[subQ1,subQ0]})])]});}
            var Q8;
            {var subQ0=sQuery(id+"F0.wireOp",EDGE,"E10.left");var subQ1=sQuery(id+"F0.wireOp",EDGE,"E0");Q8=makeQuery(id+"F1.opExtrude","SWEPT_EDGE",EDGE,{"disambiguationData":[OSD([subQ1,subQ0]),TDD([makeQuery(id+"F0.imprint","INTERSECT",VERTEX,{"disambiguationData":[OD(1.0)],"derivedFrom":[subQ1,subQ0]})])]});}
            var Q9;
            {var subQ0=sQuery(id+"F0.wireOp",EDGE,"E11.right");var subQ1=sQuery(id+"F0.wireOp",EDGE,"E0");Q9=makeQuery(id+"F1.opExtrude","SWEPT_EDGE",EDGE,{"disambiguationData":[OSD([subQ1,subQ0]),TDD([makeQuery(id+"F0.imprint","INTERSECT",VERTEX,{"disambiguationData":[OD(1.0)],"derivedFrom":[subQ1,subQ0]})])]});}
            var Q10;
            {var subQ0=sQuery(id+"F0.wireOp",EDGE,"E8.right");var subQ1=sQuery(id+"F0.wireOp",EDGE,"E0");Q10=makeQuery(id+"F1.opExtrude","SWEPT_EDGE",EDGE,{"disambiguationData":[OSD([subQ1,subQ0]),TDD([makeQuery(id+"F0.imprint","INTERSECT",VERTEX,{"disambiguationData":[OD(1.0)],"derivedFrom":[subQ1,subQ0]})])]});}
            var Q11;
            {var subQ0=sQuery(id+"F0.wireOp",EDGE,"E9.top");var subQ1=sQuery(id+"F0.wireOp",EDGE,"E0");Q11=makeQuery(id+"F1.opExtrude","SWEPT_EDGE",EDGE,{"disambiguationData":[OSD([subQ1,subQ0]),TDD([makeQuery(id+"F0.imprint","INTERSECT",VERTEX,{"disambiguationData":[OD(1.0)],"derivedFrom":[subQ1,subQ0]})])]});}
            var Q12;
            {var subQ0=sQuery(id+"F0.wireOp",EDGE,"E10.right");var subQ1=sQuery(id+"F0.wireOp",EDGE,"E0");Q12=makeQuery(id+"F1.opExtrude","SWEPT_EDGE",EDGE,{"disambiguationData":[OSD([subQ1,subQ0]),TDD([makeQuery(id+"F0.imprint","INTERSECT",VERTEX,{"disambiguationData":[OD(1.0)],"derivedFrom":[subQ1,subQ0]})])]});}
            var Q13;
            {var subQ0=sQuery(id+"F0.wireOp",EDGE,"E11.left");var subQ1=sQuery(id+"F0.wireOp",EDGE,"E0");Q13=makeQuery(id+"F1.opExtrude","SWEPT_EDGE",EDGE,{"disambiguationData":[OSD([subQ1,subQ0]),TDD([makeQuery(id+"F0.imprint","INTERSECT",VERTEX,{"disambiguationData":[OD(1.0)],"derivedFrom":[subQ1,subQ0]})])]});}
            var Q14;
            {var subQ0=sQuery(id+"F0.wireOp",EDGE,"E8.left");var subQ1=sQuery(id+"F0.wireOp",EDGE,"E0");Q14=makeQuery(id+"F1.opExtrude","SWEPT_EDGE",EDGE,{"disambiguationData":[OSD([subQ1,subQ0]),TDD([makeQuery(id+"F0.imprint","INTERSECT",VERTEX,{"disambiguationData":[OD(1.0)],"derivedFrom":[subQ1,subQ0]})])]});}
            var Q15;
            {var subQ0=sQuery(id+"F0.wireOp",EDGE,"E9.bottom");var subQ1=sQuery(id+"F0.wireOp",EDGE,"E0");Q15=makeQuery(id+"F1.opExtrude","SWEPT_EDGE",EDGE,{"disambiguationData":[OSD([subQ1,subQ0]),TDD([makeQuery(id+"F0.imprint","INTERSECT",VERTEX,{"disambiguationData":[OD(1.0)],"derivedFrom":[subQ1,subQ0]})])]});}
            var Q16;
            {var subQ0=sQuery(id+"F0.wireOp",EDGE,"E22.left");var subQ1=sQuery(id+"F0.wireOp",EDGE,"E0");Q16=makeQuery(id+"F1.opExtrude","SWEPT_EDGE",EDGE,{"disambiguationData":[OSD([subQ1,subQ0]),TDD([makeQuery(id+"F0.imprint","INTERSECT",VERTEX,{"disambiguationData":[OD(0.0)],"derivedFrom":[subQ1,subQ0]})])]});}
            var Q17;
            {var subQ0=sQuery(id+"F0.wireOp",EDGE,"E21.left");var subQ1=sQuery(id+"F0.wireOp",EDGE,"E0");Q17=makeQuery(id+"F1.opExtrude","SWEPT_EDGE",EDGE,{"disambiguationData":[OSD([subQ1,subQ0]),TDD([makeQuery(id+"F0.imprint","INTERSECT",VERTEX,{"disambiguationData":[OD(0.0)],"derivedFrom":[subQ1,subQ0]})])]});}
            var Q18;
            {var subQ0=sQuery(id+"F0.wireOp",EDGE,"E20.left");var subQ1=sQuery(id+"F0.wireOp",EDGE,"E0");Q18=makeQuery(id+"F1.opExtrude","SWEPT_EDGE",EDGE,{"disambiguationData":[OSD([subQ1,subQ0]),TDD([makeQuery(id+"F0.imprint","INTERSECT",VERTEX,{"disambiguationData":[OD(0.0)],"derivedFrom":[subQ1,subQ0]})])]});}
            var Q19;
            {var subQ0=sQuery(id+"F0.wireOp",EDGE,"E19.left");var subQ1=sQuery(id+"F0.wireOp",EDGE,"E0");Q19=makeQuery(id+"F1.opExtrude","SWEPT_EDGE",EDGE,{"disambiguationData":[OSD([subQ1,subQ0]),TDD([makeQuery(id+"F0.imprint","INTERSECT",VERTEX,{"disambiguationData":[OD(0.0)],"derivedFrom":[subQ1,subQ0]})])]});}
            var Q20;
            {var subQ0=sQuery(id+"F0.wireOp",EDGE,"E18.right");var subQ1=sQuery(id+"F0.wireOp",EDGE,"E0");Q20=makeQuery(id+"F1.opExtrude","SWEPT_EDGE",EDGE,{"disambiguationData":[OSD([subQ1,subQ0]),TDD([makeQuery(id+"F0.imprint","INTERSECT",VERTEX,{"disambiguationData":[OD(0.0)],"derivedFrom":[subQ1,subQ0]})])]});}
            var Q21;
            {var subQ0=sQuery(id+"F0.wireOp",EDGE,"E17.right");var subQ1=sQuery(id+"F0.wireOp",EDGE,"E0");Q21=makeQuery(id+"F1.opExtrude","SWEPT_EDGE",EDGE,{"disambiguationData":[OSD([subQ1,subQ0]),TDD([makeQuery(id+"F0.imprint","INTERSECT",VERTEX,{"disambiguationData":[OD(0.0)],"derivedFrom":[subQ1,subQ0]})])]});}
            var Q22;
            {var subQ0=sQuery(id+"F0.wireOp",EDGE,"E12.left");var subQ1=sQuery(id+"F0.wireOp",EDGE,"E0");Q22=makeQuery(id+"F1.opExtrude","SWEPT_EDGE",EDGE,{"disambiguationData":[OSD([subQ1,subQ0]),TDD([makeQuery(id+"F0.imprint","INTERSECT",VERTEX,{"disambiguationData":[OD(0.0)],"derivedFrom":[subQ1,subQ0]})])]});}
            var Q23;
            {var subQ0=sQuery(id+"F0.wireOp",EDGE,"E13.right");var subQ1=sQuery(id+"F0.wireOp",EDGE,"E0");Q23=makeQuery(id+"F1.opExtrude","SWEPT_EDGE",EDGE,{"disambiguationData":[OSD([subQ1,subQ0]),TDD([makeQuery(id+"F0.imprint","INTERSECT",VERTEX,{"disambiguationData":[OD(0.0)],"derivedFrom":[subQ1,subQ0]})])]});}
            var Q24;
            {var subQ0=sQuery(id+"F0.wireOp",EDGE,"E14.left");var subQ1=sQuery(id+"F0.wireOp",EDGE,"E0");Q24=makeQuery(id+"F1.opExtrude","SWEPT_EDGE",EDGE,{"disambiguationData":[OSD([subQ1,subQ0]),TDD([makeQuery(id+"F0.imprint","INTERSECT",VERTEX,{"disambiguationData":[OD(0.0)],"derivedFrom":[subQ1,subQ0]})])]});}
            var Q25;
            {var subQ0=sQuery(id+"F0.wireOp",EDGE,"E15.left");var subQ1=sQuery(id+"F0.wireOp",EDGE,"E0");Q25=makeQuery(id+"F1.opExtrude","SWEPT_EDGE",EDGE,{"disambiguationData":[OSD([subQ1,subQ0]),TDD([makeQuery(id+"F0.imprint","INTERSECT",VERTEX,{"disambiguationData":[OD(0.0)],"derivedFrom":[subQ1,subQ0]})])]});}
            var Q26;
            {var subQ0=sQuery(id+"F0.wireOp",EDGE,"E16.right");var subQ1=sQuery(id+"F0.wireOp",EDGE,"E0");Q26=makeQuery(id+"F1.opExtrude","SWEPT_EDGE",EDGE,{"disambiguationData":[OSD([subQ1,subQ0]),TDD([makeQuery(id+"F0.imprint","INTERSECT",VERTEX,{"disambiguationData":[OD(1.0)],"derivedFrom":[subQ1,subQ0]})])]});}
            var Q27;
            {var subQ0=sQuery(id+"F0.wireOp",EDGE,"E17.left");var subQ1=sQuery(id+"F0.wireOp",EDGE,"E0");Q27=makeQuery(id+"F1.opExtrude","SWEPT_EDGE",EDGE,{"disambiguationData":[OSD([subQ1,subQ0]),TDD([makeQuery(id+"F0.imprint","INTERSECT",VERTEX,{"disambiguationData":[OD(1.0)],"derivedFrom":[subQ1,subQ0]})])]});}
            var Q28;
            {var subQ0=sQuery(id+"F0.wireOp",EDGE,"E18.left");var subQ1=sQuery(id+"F0.wireOp",EDGE,"E0");Q28=makeQuery(id+"F1.opExtrude","SWEPT_EDGE",EDGE,{"disambiguationData":[OSD([subQ1,subQ0]),TDD([makeQuery(id+"F0.imprint","INTERSECT",VERTEX,{"disambiguationData":[OD(1.0)],"derivedFrom":[subQ1,subQ0]})])]});}
            var Q29;
            {var subQ0=sQuery(id+"F0.wireOp",EDGE,"E19.right");var subQ1=sQuery(id+"F0.wireOp",EDGE,"E0");Q29=makeQuery(id+"F1.opExtrude","SWEPT_EDGE",EDGE,{"disambiguationData":[OSD([subQ1,subQ0]),TDD([makeQuery(id+"F0.imprint","INTERSECT",VERTEX,{"disambiguationData":[OD(1.0)],"derivedFrom":[subQ1,subQ0]})])]});}
            var Q30;
            {var subQ0=sQuery(id+"F0.wireOp",EDGE,"E21.left");var subQ1=sQuery(id+"F0.wireOp",EDGE,"E0");Q30=makeQuery(id+"F1.opExtrude","SWEPT_EDGE",EDGE,{"disambiguationData":[OSD([subQ1,subQ0]),TDD([makeQuery(id+"F0.imprint","INTERSECT",VERTEX,{"disambiguationData":[OD(1.0)],"derivedFrom":[subQ1,subQ0]})])]});}
            var Q31;
            {var subQ0=sQuery(id+"F0.wireOp",EDGE,"E22.left");var subQ1=sQuery(id+"F0.wireOp",EDGE,"E0");Q31=makeQuery(id+"F1.opExtrude","SWEPT_EDGE",EDGE,{"disambiguationData":[OSD([subQ1,subQ0]),TDD([makeQuery(id+"F0.imprint","INTERSECT",VERTEX,{"disambiguationData":[OD(1.0)],"derivedFrom":[subQ1,subQ0]})])]});}
            var Q32;
            {var subQ0=sQuery(id+"F0.wireOp",EDGE,"E12.right");var subQ1=sQuery(id+"F0.wireOp",EDGE,"E0");Q32=makeQuery(id+"F1.opExtrude","SWEPT_EDGE",EDGE,{"disambiguationData":[OSD([subQ1,subQ0]),TDD([makeQuery(id+"F0.imprint","INTERSECT",VERTEX,{"disambiguationData":[OD(1.0)],"derivedFrom":[subQ1,subQ0]})])]});}
            var Q33;
            {var subQ0=sQuery(id+"F0.wireOp",EDGE,"E20.right");var subQ1=sQuery(id+"F0.wireOp",EDGE,"E0");Q33=makeQuery(id+"F1.opExtrude","SWEPT_EDGE",EDGE,{"disambiguationData":[OSD([subQ1,subQ0]),TDD([makeQuery(id+"F0.imprint","INTERSECT",VERTEX,{"disambiguationData":[OD(1.0)],"derivedFrom":[subQ1,subQ0]})])]});}
            var Q34;
            {var subQ0=sQuery(id+"F0.wireOp",EDGE,"E13.left");var subQ1=sQuery(id+"F0.wireOp",EDGE,"E0");Q34=makeQuery(id+"F1.opExtrude","SWEPT_EDGE",EDGE,{"disambiguationData":[OSD([subQ1,subQ0]),TDD([makeQuery(id+"F0.imprint","INTERSECT",VERTEX,{"disambiguationData":[OD(1.0)],"derivedFrom":[subQ1,subQ0]})])]});}
            var Q35;
            {var subQ0=sQuery(id+"F0.wireOp",EDGE,"E14.right");var subQ1=sQuery(id+"F0.wireOp",EDGE,"E0");Q35=makeQuery(id+"F1.opExtrude","SWEPT_EDGE",EDGE,{"disambiguationData":[OSD([subQ1,subQ0]),TDD([makeQuery(id+"F0.imprint","INTERSECT",VERTEX,{"disambiguationData":[OD(1.0)],"derivedFrom":[subQ1,subQ0]})])]});}
            var Q36;
            {var subQ0=sQuery(id+"F0.wireOp",EDGE,"E21.right");var subQ1=sQuery(id+"F0.wireOp",EDGE,"E0");Q36=makeQuery(id+"F1.opExtrude","SWEPT_EDGE",EDGE,{"disambiguationData":[OSD([subQ1,subQ0]),TDD([makeQuery(id+"F0.imprint","INTERSECT",VERTEX,{"disambiguationData":[OD(1.0)],"derivedFrom":[subQ1,subQ0]})])]});}
            var Q37;
            {var subQ0=sQuery(id+"F0.wireOp",EDGE,"E22.right");var subQ1=sQuery(id+"F0.wireOp",EDGE,"E0");Q37=makeQuery(id+"F1.opExtrude","SWEPT_EDGE",EDGE,{"disambiguationData":[OSD([subQ1,subQ0]),TDD([makeQuery(id+"F0.imprint","INTERSECT",VERTEX,{"disambiguationData":[OD(1.0)],"derivedFrom":[subQ1,subQ0]})])]});}
            var Q38;
            {var subQ0=sQuery(id+"F0.wireOp",EDGE,"E22.right");var subQ1=sQuery(id+"F0.wireOp",EDGE,"E0");Q38=makeQuery(id+"F1.opExtrude","SWEPT_EDGE",EDGE,{"disambiguationData":[OSD([subQ1,subQ0]),TDD([makeQuery(id+"F0.imprint","INTERSECT",VERTEX,{"disambiguationData":[OD(0.0)],"derivedFrom":[subQ1,subQ0]})])]});}
            var Q39;
            {var subQ0=sQuery(id+"F0.wireOp",EDGE,"E21.right");var subQ1=sQuery(id+"F0.wireOp",EDGE,"E0");Q39=makeQuery(id+"F1.opExtrude","SWEPT_EDGE",EDGE,{"disambiguationData":[OSD([subQ1,subQ0]),TDD([makeQuery(id+"F0.imprint","INTERSECT",VERTEX,{"disambiguationData":[OD(0.0)],"derivedFrom":[subQ1,subQ0]})])]});}
            var Q40;
            {var subQ0=sQuery(id+"F0.wireOp",EDGE,"E20.right");var subQ1=sQuery(id+"F0.wireOp",EDGE,"E0");Q40=makeQuery(id+"F1.opExtrude","SWEPT_EDGE",EDGE,{"disambiguationData":[OSD([subQ1,subQ0]),TDD([makeQuery(id+"F0.imprint","INTERSECT",VERTEX,{"disambiguationData":[OD(0.0)],"derivedFrom":[subQ1,subQ0]})])]});}
            var Q41;
            {var subQ0=sQuery(id+"F0.wireOp",EDGE,"E15.right");var subQ1=sQuery(id+"F0.wireOp",EDGE,"E0");Q41=makeQuery(id+"F1.opExtrude","SWEPT_EDGE",EDGE,{"disambiguationData":[OSD([subQ1,subQ0]),TDD([makeQuery(id+"F0.imprint","INTERSECT",VERTEX,{"disambiguationData":[OD(1.0)],"derivedFrom":[subQ1,subQ0]})])]});}
            var Q42;
            {var subQ0=sQuery(id+"F0.wireOp",EDGE,"E16.left");var subQ1=sQuery(id+"F0.wireOp",EDGE,"E0");Q42=makeQuery(id+"F1.opExtrude","SWEPT_EDGE",EDGE,{"disambiguationData":[OSD([subQ1,subQ0]),TDD([makeQuery(id+"F0.imprint","INTERSECT",VERTEX,{"disambiguationData":[OD(0.0)],"derivedFrom":[subQ1,subQ0]})])]});}
            var Q43;
            {var subQ0=sQuery(id+"F0.wireOp",EDGE,"E14.left");var subQ1=sQuery(id+"F0.wireOp",EDGE,"E0");Q43=makeQuery(id+"F1.opExtrude","SWEPT_EDGE",EDGE,{"disambiguationData":[OSD([subQ1,subQ0]),TDD([makeQuery(id+"F0.imprint","INTERSECT",VERTEX,{"disambiguationData":[OD(1.0)],"derivedFrom":[subQ1,subQ0]})])]});}
            var Q44;
            {var subQ0=sQuery(id+"F0.wireOp",EDGE,"E19.right");var subQ1=sQuery(id+"F0.wireOp",EDGE,"E0");Q44=makeQuery(id+"F1.opExtrude","SWEPT_EDGE",EDGE,{"disambiguationData":[OSD([subQ1,subQ0]),TDD([makeQuery(id+"F0.imprint","INTERSECT",VERTEX,{"disambiguationData":[OD(0.0)],"derivedFrom":[subQ1,subQ0]})])]});}
            var Q45;
            {var subQ0=sQuery(id+"F0.wireOp",EDGE,"E18.left");var subQ1=sQuery(id+"F0.wireOp",EDGE,"E0");Q45=makeQuery(id+"F1.opExtrude","SWEPT_EDGE",EDGE,{"disambiguationData":[OSD([subQ1,subQ0]),TDD([makeQuery(id+"F0.imprint","INTERSECT",VERTEX,{"disambiguationData":[OD(0.0)],"derivedFrom":[subQ1,subQ0]})])]});}
            var Q46;
            {var subQ0=sQuery(id+"F0.wireOp",EDGE,"E15.left");var subQ1=sQuery(id+"F0.wireOp",EDGE,"E0");Q46=makeQuery(id+"F1.opExtrude","SWEPT_EDGE",EDGE,{"disambiguationData":[OSD([subQ1,subQ0]),TDD([makeQuery(id+"F0.imprint","INTERSECT",VERTEX,{"disambiguationData":[OD(1.0)],"derivedFrom":[subQ1,subQ0]})])]});}
            var Q47;
            {var subQ0=sQuery(id+"F0.wireOp",EDGE,"E16.right");var subQ1=sQuery(id+"F0.wireOp",EDGE,"E0");Q47=makeQuery(id+"F1.opExtrude","SWEPT_EDGE",EDGE,{"disambiguationData":[OSD([subQ1,subQ0]),TDD([makeQuery(id+"F0.imprint","INTERSECT",VERTEX,{"disambiguationData":[OD(0.0)],"derivedFrom":[subQ1,subQ0]})])]});}
            var Q48;
            {var subQ0=sQuery(id+"F0.wireOp",EDGE,"E12.left");var subQ1=sQuery(id+"F0.wireOp",EDGE,"E0");Q48=makeQuery(id+"F1.opExtrude","SWEPT_EDGE",EDGE,{"disambiguationData":[OSD([subQ1,subQ0]),TDD([makeQuery(id+"F0.imprint","INTERSECT",VERTEX,{"disambiguationData":[OD(1.0)],"derivedFrom":[subQ1,subQ0]})])]});}
            var Q49;
            {var subQ0=sQuery(id+"F0.wireOp",EDGE,"E13.right");var subQ1=sQuery(id+"F0.wireOp",EDGE,"E0");Q49=makeQuery(id+"F1.opExtrude","SWEPT_EDGE",EDGE,{"disambiguationData":[OSD([subQ1,subQ0]),TDD([makeQuery(id+"F0.imprint","INTERSECT",VERTEX,{"disambiguationData":[OD(1.0)],"derivedFrom":[subQ1,subQ0]})])]});}
            var Q50;
            {var subQ0=sQuery(id+"F0.wireOp",EDGE,"E19.left");var subQ1=sQuery(id+"F0.wireOp",EDGE,"E0");Q50=makeQuery(id+"F1.opExtrude","SWEPT_EDGE",EDGE,{"disambiguationData":[OSD([subQ1,subQ0]),TDD([makeQuery(id+"F0.imprint","INTERSECT",VERTEX,{"disambiguationData":[OD(1.0)],"derivedFrom":[subQ1,subQ0]})])]});}
            var Q51;
            {var subQ0=sQuery(id+"F0.wireOp",EDGE,"E17.right");var subQ1=sQuery(id+"F0.wireOp",EDGE,"E0");Q51=makeQuery(id+"F1.opExtrude","SWEPT_EDGE",EDGE,{"disambiguationData":[OSD([subQ1,subQ0]),TDD([makeQuery(id+"F0.imprint","INTERSECT",VERTEX,{"disambiguationData":[OD(1.0)],"derivedFrom":[subQ1,subQ0]})])]});}
            var Q52;
            {var subQ0=sQuery(id+"F0.wireOp",EDGE,"E13.left");var subQ1=sQuery(id+"F0.wireOp",EDGE,"E0");Q52=makeQuery(id+"F1.opExtrude","SWEPT_EDGE",EDGE,{"disambiguationData":[OSD([subQ1,subQ0]),TDD([makeQuery(id+"F0.imprint","INTERSECT",VERTEX,{"disambiguationData":[OD(0.0)],"derivedFrom":[subQ1,subQ0]})])]});}
            var Q53;
            {var subQ0=sQuery(id+"F0.wireOp",EDGE,"E12.right");var subQ1=sQuery(id+"F0.wireOp",EDGE,"E0");Q53=makeQuery(id+"F1.opExtrude","SWEPT_EDGE",EDGE,{"disambiguationData":[OSD([subQ1,subQ0]),TDD([makeQuery(id+"F0.imprint","INTERSECT",VERTEX,{"disambiguationData":[OD(0.0)],"derivedFrom":[subQ1,subQ0]})])]});}
            var Q54;
            {var subQ0=sQuery(id+"F0.wireOp",EDGE,"E14.right");var subQ1=sQuery(id+"F0.wireOp",EDGE,"E0");Q54=makeQuery(id+"F1.opExtrude","SWEPT_EDGE",EDGE,{"disambiguationData":[OSD([subQ1,subQ0]),TDD([makeQuery(id+"F0.imprint","INTERSECT",VERTEX,{"disambiguationData":[OD(0.0)],"derivedFrom":[subQ1,subQ0]})])]});}
            var Q55;
            {var subQ0=sQuery(id+"F0.wireOp",EDGE,"E18.right");var subQ1=sQuery(id+"F0.wireOp",EDGE,"E0");Q55=makeQuery(id+"F1.opExtrude","SWEPT_EDGE",EDGE,{"disambiguationData":[OSD([subQ1,subQ0]),TDD([makeQuery(id+"F0.imprint","INTERSECT",VERTEX,{"disambiguationData":[OD(1.0)],"derivedFrom":[subQ1,subQ0]})])]});}
            var Q56;
            {var subQ0=sQuery(id+"F0.wireOp",EDGE,"E16.left");var subQ1=sQuery(id+"F0.wireOp",EDGE,"E0");Q56=makeQuery(id+"F1.opExtrude","SWEPT_EDGE",EDGE,{"disambiguationData":[OSD([subQ1,subQ0]),TDD([makeQuery(id+"F0.imprint","INTERSECT",VERTEX,{"disambiguationData":[OD(1.0)],"derivedFrom":[subQ1,subQ0]})])]});}
            var Q57;
            {var subQ0=sQuery(id+"F0.wireOp",EDGE,"E15.right");var subQ1=sQuery(id+"F0.wireOp",EDGE,"E0");Q57=makeQuery(id+"F1.opExtrude","SWEPT_EDGE",EDGE,{"disambiguationData":[OSD([subQ1,subQ0]),TDD([makeQuery(id+"F0.imprint","INTERSECT",VERTEX,{"disambiguationData":[OD(0.0)],"derivedFrom":[subQ1,subQ0]})])]});}
            var Q58;
            {var subQ0=sQuery(id+"F0.wireOp",EDGE,"E20.left");var subQ1=sQuery(id+"F0.wireOp",EDGE,"E0");Q58=makeQuery(id+"F1.opExtrude","SWEPT_EDGE",EDGE,{"disambiguationData":[OSD([subQ1,subQ0]),TDD([makeQuery(id+"F0.imprint","INTERSECT",VERTEX,{"disambiguationData":[OD(1.0)],"derivedFrom":[subQ1,subQ0]})])]});}
            var Q59;
            {var subQ0=sQuery(id+"F0.wireOp",EDGE,"E17.left");var subQ1=sQuery(id+"F0.wireOp",EDGE,"E0");Q59=makeQuery(id+"F1.opExtrude","SWEPT_EDGE",EDGE,{"disambiguationData":[OSD([subQ1,subQ0]),TDD([makeQuery(id+"F0.imprint","INTERSECT",VERTEX,{"disambiguationData":[OD(0.0)],"derivedFrom":[subQ1,subQ0]})])]});}
            fillet(context, id + "F3", {"entities" : qUnion([Q0, Q1, Q2, Q3, Q4, Q5, Q6, Q7, Q8, Q9, Q10, Q11, Q12, Q13, Q14, Q15, Q16, Q17, Q18, Q19, Q20, Q21, Q22, Q23, Q24, Q25, Q26, Q27, Q28, Q29, Q30, Q31, Q32, Q33, Q34, Q35, Q36, Q37, Q38, Q39, Q40, Q41, Q42, Q43, Q44, Q45, Q46, Q47, Q48, Q49, Q50, Q51, Q52, Q53, Q54, Q55, Q56, Q57, Q58, Q59]), "radius" : 3 * mm, "tangentPropagation" : true, "allowEdgeOverflow" : false});
        }
        {
            var Q0;
            Q0=qCreatedBy(makeId("Top.planeOp"),FACE);
            var sketch = newSketch(context, id + "F4", { "sketchPlane" : qUnion([Q0])});
            skCircle(sketch, "E23", {"center": v(0, 0) * mm, "radius": 56 * mm});
            skCircle(sketch, "E24", {"center": v(0, 0) * mm, "radius": 55 * mm});
            skLineSegment(sketch, "E25", {"start": v(0, 75.16) * mm, "end": v(0, -75.72) * mm, "construction": true});
            skLineSegment(sketch, "E26", {"start": v(-78.17, 0) * mm, "end": v(81.81, 0) * mm, "construction": true});
            skLineSegment(sketch, "E27", {"start": v(0, 0) * mm, "end": v(-70.05, 40.44) * mm, "construction": true});
            skLineSegment(sketch, "E28", {"start": v(0, 0) * mm, "end": v(72.4, -41.8) * mm, "construction": true});
            skLineSegment(sketch, "E29", {"start": v(0, 0) * mm, "end": v(70.53, 40.72) * mm, "construction": true});
            skLineSegment(sketch, "E30", {"start": v(0, 0) * mm, "end": v(-71.48, -41.27) * mm, "construction": true});
            skCircle(sketch, "E31", {"center": v(0, 56) * mm, "radius": 2.25 * mm});
            skCircle(sketch, "E32", {"center": v(0, 56) * mm, "radius": 1 * mm});
            skCircle(sketch, "E33", {"center": v(0, -56) * mm, "radius": 2.25 * mm});
            skLineSegment(sketch, "E34.bottom", {"start": v(0, -57.27) * mm, "end": v(-1.27, -56) * mm});
            skLineSegment(sketch, "E34.top", {"start": v(1.27, -56) * mm, "end": v(0, -54.73) * mm});
            skLineSegment(sketch, "E34.left", {"start": v(0, -57.27) * mm, "end": v(1.27, -56) * mm});
            skLineSegment(sketch, "E34.right", {"start": v(-1.27, -56) * mm, "end": v(0, -54.73) * mm});
            skCircle(sketch, "E35", {"center": v(-48.5, -28) * mm, "radius": 2.25 * mm});
            skCircle(sketch, "E36", {"center": v(-48.5, -28) * mm, "radius": 1 * mm});
            skCircle(sketch, "E37", {"center": v(-48.5, 28) * mm, "radius": 2.25 * mm});
            skCircle(sketch, "E38", {"center": v(-48.5, 28) * mm, "radius": 1 * mm});
            skCircle(sketch, "E39", {"center": v(48.5, 28) * mm, "radius": 2.25 * mm});
            skCircle(sketch, "E40", {"center": v(48.5, 28) * mm, "radius": 1 * mm});
            skCircle(sketch, "E41", {"center": v(48.5, -28) * mm, "radius": 2.25 * mm});
            skCircle(sketch, "E42", {"center": v(48.5, -28) * mm, "radius": 1 * mm});
            skSolve(sketch);
        }
        {
            var Q0;
            {var subQ0=sQuery(id+"F4.wireOp",EDGE,"E41");var subQ1=sQuery(id+"F4.wireOp",EDGE,"E23");var subQ2=makeQuery(id+"F4.imprint","INTERSECT",VERTEX,{"disambiguationData":[OD(0.0)],"derivedFrom":[subQ1,subQ0]});Q0=makeQuery(id+"F4.imprint","IMPRINT",FACE,{"disambiguationData":[TD([[makeQuery(id+"F4.imprint","IMPRINT",EDGE,{"disambiguationData":[TD([[subQ2,-1.0]])],"derivedFrom":subQ1}),-1.0]])]});}
            var Q1;
            {var subQ0=sQuery(id+"F4.wireOp",EDGE,"E41");var subQ1=sQuery(id+"F4.wireOp",EDGE,"E23");var subQ2=makeQuery(id+"F4.imprint","INTERSECT",VERTEX,{"disambiguationData":[OD(1.0)],"derivedFrom":[subQ1,subQ0]});Q1=makeQuery(id+"F4.imprint","IMPRINT",FACE,{"disambiguationData":[TD([[makeQuery(id+"F4.imprint","IMPRINT",EDGE,{"disambiguationData":[TD([[subQ2,1.0]])],"derivedFrom":subQ1}),1.0]])]});}
            var Q2;
            {var subQ0=sQuery(id+"F4.wireOp",EDGE,"E41");var subQ1=sQuery(id+"F4.wireOp",EDGE,"E23");var subQ2=makeQuery(id+"F4.imprint","INTERSECT",VERTEX,{"disambiguationData":[OD(0.0)],"derivedFrom":[subQ1,subQ0]});Q2=makeQuery(id+"F4.imprint","IMPRINT",FACE,{"disambiguationData":[TD([[makeQuery(id+"F4.imprint","IMPRINT",EDGE,{"disambiguationData":[TD([[subQ2,-1.0]])],"derivedFrom":subQ1}),1.0]])]});}
            var Q3;
            {var subQ0=sQuery(id+"F4.wireOp",EDGE,"E41");var subQ1=sQuery(id+"F4.wireOp",EDGE,"E24");var subQ2=makeQuery(id+"F4.imprint","INTERSECT",VERTEX,{"disambiguationData":[OD(0.0)],"derivedFrom":[subQ1,subQ0]});Q3=makeQuery(id+"F4.imprint","IMPRINT",FACE,{"disambiguationData":[TD([[makeQuery(id+"F4.imprint","IMPRINT",EDGE,{"disambiguationData":[TD([[subQ2,-1.0]])],"derivedFrom":subQ1}),1.0]])]});}
            var Q4;
            {var subQ0=sQuery(id+"F4.wireOp",EDGE,"E39");var subQ1=sQuery(id+"F4.wireOp",EDGE,"E23");var subQ2=makeQuery(id+"F4.imprint","INTERSECT",VERTEX,{"disambiguationData":[OD(0.0)],"derivedFrom":[subQ1,subQ0]});Q4=makeQuery(id+"F4.imprint","IMPRINT",FACE,{"disambiguationData":[TD([[makeQuery(id+"F4.imprint","IMPRINT",EDGE,{"disambiguationData":[TD([[subQ2,-1.0]])],"derivedFrom":subQ1}),-1.0]])]});}
            var Q5;
            {var subQ0=sQuery(id+"F4.wireOp",EDGE,"E24");var subQ1=makeQuery(id+"F4.imprint","INTERSECT",VERTEX,{"derivedFrom":[subQ0,sQuery(id+"F4.wireOp",EDGE,"E40")]});Q5=makeQuery(id+"F4.imprint","IMPRINT",FACE,{"disambiguationData":[TD([[makeQuery(id+"F4.imprint","IMPRINT",EDGE,{"disambiguationData":[TD([[subQ1,1.0]])],"derivedFrom":subQ0}),1.0]])]});}
            var Q6;
            {var subQ0=sQuery(id+"F4.wireOp",EDGE,"E39");var subQ1=sQuery(id+"F4.wireOp",EDGE,"E23");var subQ2=makeQuery(id+"F4.imprint","INTERSECT",VERTEX,{"disambiguationData":[OD(1.0)],"derivedFrom":[subQ1,subQ0]});Q6=makeQuery(id+"F4.imprint","IMPRINT",FACE,{"disambiguationData":[TD([[makeQuery(id+"F4.imprint","IMPRINT",EDGE,{"disambiguationData":[TD([[subQ2,1.0]])],"derivedFrom":subQ1}),1.0]])]});}
            var Q7;
            {var subQ0=sQuery(id+"F4.wireOp",EDGE,"E39");var subQ1=sQuery(id+"F4.wireOp",EDGE,"E23");var subQ2=makeQuery(id+"F4.imprint","INTERSECT",VERTEX,{"disambiguationData":[OD(0.0)],"derivedFrom":[subQ1,subQ0]});Q7=makeQuery(id+"F4.imprint","IMPRINT",FACE,{"disambiguationData":[TD([[makeQuery(id+"F4.imprint","IMPRINT",EDGE,{"disambiguationData":[TD([[subQ2,-1.0]])],"derivedFrom":subQ1}),1.0]])]});}
            var Q8;
            {var subQ0=sQuery(id+"F4.wireOp",EDGE,"E34.bottom");Q8=makeQuery(id+"F4.imprint","IMPRINT",FACE,{"disambiguationData":[TD([[makeQuery(id+"F4.imprint","IMPRINT",EDGE,{"derivedFrom":subQ0}),1.0]])]});}
            var Q9;
            {var subQ0=sQuery(id+"F4.wireOp",EDGE,"E33");var subQ1=sQuery(id+"F4.wireOp",EDGE,"E23");var subQ2=makeQuery(id+"F4.imprint","INTERSECT",VERTEX,{"disambiguationData":[OD(1.0)],"derivedFrom":[subQ1,subQ0]});Q9=makeQuery(id+"F4.imprint","IMPRINT",FACE,{"disambiguationData":[TD([[makeQuery(id+"F4.imprint","IMPRINT",EDGE,{"disambiguationData":[TD([[subQ2,1.0]])],"derivedFrom":subQ1}),1.0]])]});}
            var Q10;
            {var subQ0=sQuery(id+"F4.wireOp",EDGE,"E33");var subQ1=sQuery(id+"F4.wireOp",EDGE,"E23");var subQ2=makeQuery(id+"F4.imprint","INTERSECT",VERTEX,{"disambiguationData":[OD(0.0)],"derivedFrom":[subQ1,subQ0]});Q10=makeQuery(id+"F4.imprint","IMPRINT",FACE,{"disambiguationData":[TD([[makeQuery(id+"F4.imprint","IMPRINT",EDGE,{"disambiguationData":[TD([[subQ2,-1.0]])],"derivedFrom":subQ1}),1.0]])]});}
            var Q11;
            {var subQ3=sQuery(id+"F4.wireOp",EDGE,"E24");var subQ5=sQuery(id+"F4.wireOp",EDGE,"E33");var subQ7=makeQuery(id+"F4.imprint","INTERSECT",VERTEX,{"disambiguationData":[OD(0.0)],"derivedFrom":[subQ3,subQ5]});Q11=makeQuery(id+"F4.imprint","IMPRINT",FACE,{"disambiguationData":[TD([[makeQuery(id+"F4.imprint","IMPRINT",EDGE,{"disambiguationData":[TD([[subQ7,-1.0]])],"derivedFrom":subQ3}),1.0]])]});}
            var Q12;
            {var subQ0=sQuery(id+"F4.wireOp",EDGE,"E35");var subQ1=sQuery(id+"F4.wireOp",EDGE,"E23");var subQ2=makeQuery(id+"F4.imprint","INTERSECT",VERTEX,{"disambiguationData":[OD(0.0)],"derivedFrom":[subQ1,subQ0]});Q12=makeQuery(id+"F4.imprint","IMPRINT",FACE,{"disambiguationData":[TD([[makeQuery(id+"F4.imprint","IMPRINT",EDGE,{"disambiguationData":[TD([[subQ2,-1.0]])],"derivedFrom":subQ1}),-1.0]])]});}
            var Q13;
            {var subQ0=sQuery(id+"F4.wireOp",EDGE,"E35");var subQ1=sQuery(id+"F4.wireOp",EDGE,"E23");var subQ2=makeQuery(id+"F4.imprint","INTERSECT",VERTEX,{"disambiguationData":[OD(0.0)],"derivedFrom":[subQ1,subQ0]});Q13=makeQuery(id+"F4.imprint","IMPRINT",FACE,{"disambiguationData":[TD([[makeQuery(id+"F4.imprint","IMPRINT",EDGE,{"disambiguationData":[TD([[subQ2,-1.0]])],"derivedFrom":subQ1}),1.0]])]});}
            var Q14;
            {var subQ0=sQuery(id+"F4.wireOp",EDGE,"E35");var subQ1=sQuery(id+"F4.wireOp",EDGE,"E23");var subQ2=makeQuery(id+"F4.imprint","INTERSECT",VERTEX,{"disambiguationData":[OD(1.0)],"derivedFrom":[subQ1,subQ0]});Q14=makeQuery(id+"F4.imprint","IMPRINT",FACE,{"disambiguationData":[TD([[makeQuery(id+"F4.imprint","IMPRINT",EDGE,{"disambiguationData":[TD([[subQ2,1.0]])],"derivedFrom":subQ1}),1.0]])]});}
            var Q15;
            {var subQ0=sQuery(id+"F4.wireOp",EDGE,"E35");var subQ1=sQuery(id+"F4.wireOp",EDGE,"E24");var subQ2=makeQuery(id+"F4.imprint","INTERSECT",VERTEX,{"disambiguationData":[OD(0.0)],"derivedFrom":[subQ1,subQ0]});Q15=makeQuery(id+"F4.imprint","IMPRINT",FACE,{"disambiguationData":[TD([[makeQuery(id+"F4.imprint","IMPRINT",EDGE,{"disambiguationData":[TD([[subQ2,-1.0]])],"derivedFrom":subQ1}),1.0]])]});}
            var Q16;
            {var subQ0=sQuery(id+"F4.wireOp",EDGE,"E37");var subQ1=sQuery(id+"F4.wireOp",EDGE,"E23");var subQ2=makeQuery(id+"F4.imprint","INTERSECT",VERTEX,{"disambiguationData":[OD(0.0)],"derivedFrom":[subQ1,subQ0]});Q16=makeQuery(id+"F4.imprint","IMPRINT",FACE,{"disambiguationData":[TD([[makeQuery(id+"F4.imprint","IMPRINT",EDGE,{"disambiguationData":[TD([[subQ2,-1.0]])],"derivedFrom":subQ1}),-1.0]])]});}
            var Q17;
            {var subQ0=sQuery(id+"F4.wireOp",EDGE,"E37");var subQ1=sQuery(id+"F4.wireOp",EDGE,"E23");var subQ2=makeQuery(id+"F4.imprint","INTERSECT",VERTEX,{"disambiguationData":[OD(0.0)],"derivedFrom":[subQ1,subQ0]});Q17=makeQuery(id+"F4.imprint","IMPRINT",FACE,{"disambiguationData":[TD([[makeQuery(id+"F4.imprint","IMPRINT",EDGE,{"disambiguationData":[TD([[subQ2,-1.0]])],"derivedFrom":subQ1}),1.0]])]});}
            var Q18;
            {var subQ0=sQuery(id+"F4.wireOp",EDGE,"E37");var subQ1=sQuery(id+"F4.wireOp",EDGE,"E23");var subQ2=makeQuery(id+"F4.imprint","INTERSECT",VERTEX,{"disambiguationData":[OD(1.0)],"derivedFrom":[subQ1,subQ0]});Q18=makeQuery(id+"F4.imprint","IMPRINT",FACE,{"disambiguationData":[TD([[makeQuery(id+"F4.imprint","IMPRINT",EDGE,{"disambiguationData":[TD([[subQ2,1.0]])],"derivedFrom":subQ1}),1.0]])]});}
            var Q19;
            {var subQ0=sQuery(id+"F4.wireOp",EDGE,"E37");var subQ1=sQuery(id+"F4.wireOp",EDGE,"E24");var subQ2=makeQuery(id+"F4.imprint","INTERSECT",VERTEX,{"disambiguationData":[OD(0.0)],"derivedFrom":[subQ1,subQ0]});Q19=makeQuery(id+"F4.imprint","IMPRINT",FACE,{"disambiguationData":[TD([[makeQuery(id+"F4.imprint","IMPRINT",EDGE,{"disambiguationData":[TD([[subQ2,-1.0]])],"derivedFrom":subQ1}),1.0]])]});}
            var Q20;
            {var subQ0=sQuery(id+"F4.wireOp",EDGE,"E31");var subQ1=sQuery(id+"F4.wireOp",EDGE,"E24");var subQ2=makeQuery(id+"F4.imprint","INTERSECT",VERTEX,{"disambiguationData":[OD(0.0)],"derivedFrom":[subQ1,subQ0]});Q20=makeQuery(id+"F4.imprint","IMPRINT",FACE,{"disambiguationData":[TD([[makeQuery(id+"F4.imprint","IMPRINT",EDGE,{"disambiguationData":[TD([[subQ2,-1.0]])],"derivedFrom":subQ1}),1.0]])]});}
            var Q21;
            {var subQ0=sQuery(id+"F4.wireOp",EDGE,"E31");var subQ1=sQuery(id+"F4.wireOp",EDGE,"E23");var subQ2=makeQuery(id+"F4.imprint","INTERSECT",VERTEX,{"disambiguationData":[OD(1.0)],"derivedFrom":[subQ1,subQ0]});Q21=makeQuery(id+"F4.imprint","IMPRINT",FACE,{"disambiguationData":[TD([[makeQuery(id+"F4.imprint","IMPRINT",EDGE,{"disambiguationData":[TD([[subQ2,1.0]])],"derivedFrom":subQ1}),1.0]])]});}
            var Q22;
            {var subQ0=sQuery(id+"F4.wireOp",EDGE,"E31");var subQ1=sQuery(id+"F4.wireOp",EDGE,"E23");var subQ2=makeQuery(id+"F4.imprint","INTERSECT",VERTEX,{"disambiguationData":[OD(0.0)],"derivedFrom":[subQ1,subQ0]});Q22=makeQuery(id+"F4.imprint","IMPRINT",FACE,{"disambiguationData":[TD([[makeQuery(id+"F4.imprint","IMPRINT",EDGE,{"disambiguationData":[TD([[subQ2,-1.0]])],"derivedFrom":subQ1}),1.0]])]});}
            var Q23;
            {var subQ0=sQuery(id+"F4.wireOp",EDGE,"E31");var subQ1=sQuery(id+"F4.wireOp",EDGE,"E23");var subQ2=makeQuery(id+"F4.imprint","INTERSECT",VERTEX,{"disambiguationData":[OD(0.0)],"derivedFrom":[subQ1,subQ0]});Q23=makeQuery(id+"F4.imprint","IMPRINT",FACE,{"disambiguationData":[TD([[makeQuery(id+"F4.imprint","IMPRINT",EDGE,{"disambiguationData":[TD([[subQ2,-1.0]])],"derivedFrom":subQ1}),-1.0]])]});}
            extrude(context, id + "F5", {"entities" : qUnion([Q0, Q1, Q2, Q3, Q4, Q5, Q6, Q7, Q8, Q9, Q10, Q11, Q12, Q13, Q14, Q15, Q16, Q17, Q18, Q19, Q20, Q21, Q22, Q23]), "operationType" : NewBodyOperationType.ADD, "depth" : 10 * mm, "offsetDistance" : 25 * mm});
        }
        {
            var Q0;
            {var subQ0=sQuery(id+"F4.wireOp",EDGE,"E32");var subQ1=sQuery(id+"F4.wireOp",EDGE,"E23");var subQ2=makeQuery(id+"F4.imprint","INTERSECT",VERTEX,{"disambiguationData":[OD(0.0)],"derivedFrom":[subQ1,subQ0]});Q0=makeQuery(id+"F4.imprint","IMPRINT",FACE,{"disambiguationData":[TD([[makeQuery(id+"F4.imprint","IMPRINT",EDGE,{"disambiguationData":[TD([[subQ2,-1.0]])],"derivedFrom":subQ1}),-1.0]])]});}
            var Q1;
            {var subQ0=sQuery(id+"F4.wireOp",EDGE,"E32");var subQ1=sQuery(id+"F4.wireOp",EDGE,"E23");var subQ2=makeQuery(id+"F4.imprint","INTERSECT",VERTEX,{"disambiguationData":[OD(0.0)],"derivedFrom":[subQ1,subQ0]});Q1=makeQuery(id+"F4.imprint","IMPRINT",FACE,{"disambiguationData":[TD([[makeQuery(id+"F4.imprint","IMPRINT",EDGE,{"disambiguationData":[TD([[subQ2,-1.0]])],"derivedFrom":subQ1}),1.0]])]});}
            var Q2;
            {var subQ0=sQuery(id+"F4.wireOp",EDGE,"E40");var subQ1=sQuery(id+"F4.wireOp",EDGE,"E23");var subQ2=makeQuery(id+"F4.imprint","INTERSECT",VERTEX,{"disambiguationData":[OD(0.0)],"derivedFrom":[subQ1,subQ0]});Q2=makeQuery(id+"F4.imprint","IMPRINT",FACE,{"disambiguationData":[TD([[makeQuery(id+"F4.imprint","IMPRINT",EDGE,{"disambiguationData":[TD([[subQ2,-1.0]])],"derivedFrom":subQ1}),1.0]])]});}
            var Q3;
            {var subQ0=sQuery(id+"F4.wireOp",EDGE,"E40");var subQ1=sQuery(id+"F4.wireOp",EDGE,"E23");var subQ2=makeQuery(id+"F4.imprint","INTERSECT",VERTEX,{"disambiguationData":[OD(0.0)],"derivedFrom":[subQ1,subQ0]});Q3=makeQuery(id+"F4.imprint","IMPRINT",FACE,{"disambiguationData":[TD([[makeQuery(id+"F4.imprint","IMPRINT",EDGE,{"disambiguationData":[TD([[subQ2,-1.0]])],"derivedFrom":subQ1}),-1.0]])]});}
            var Q4;
            {var subQ0=sQuery(id+"F4.wireOp",EDGE,"E42");var subQ1=sQuery(id+"F4.wireOp",EDGE,"E23");var subQ2=makeQuery(id+"F4.imprint","INTERSECT",VERTEX,{"disambiguationData":[OD(0.0)],"derivedFrom":[subQ1,subQ0]});Q4=makeQuery(id+"F4.imprint","IMPRINT",FACE,{"disambiguationData":[TD([[makeQuery(id+"F4.imprint","IMPRINT",EDGE,{"disambiguationData":[TD([[subQ2,-1.0]])],"derivedFrom":subQ1}),-1.0]])]});}
            var Q5;
            {var subQ0=sQuery(id+"F4.wireOp",EDGE,"E42");var subQ1=sQuery(id+"F4.wireOp",EDGE,"E23");var subQ2=makeQuery(id+"F4.imprint","INTERSECT",VERTEX,{"disambiguationData":[OD(0.0)],"derivedFrom":[subQ1,subQ0]});Q5=makeQuery(id+"F4.imprint","IMPRINT",FACE,{"disambiguationData":[TD([[makeQuery(id+"F4.imprint","IMPRINT",EDGE,{"disambiguationData":[TD([[subQ2,-1.0]])],"derivedFrom":subQ1}),1.0]])]});}
            var Q6;
            {var subQ4=sQuery(id+"F4.wireOp",EDGE,"E34.bottom");Q6=makeQuery(id+"F4.imprint","IMPRINT",FACE,{"disambiguationData":[TD([[makeQuery(id+"F4.imprint","IMPRINT",EDGE,{"derivedFrom":subQ4}),-1.0]])]});}
            var Q7;
            {var subQ0=sQuery(id+"F4.wireOp",EDGE,"E34.right");var subQ1=sQuery(id+"F4.wireOp",EDGE,"E23");var subQ2=makeQuery(id+"F4.imprint","INTERSECT",VERTEX,{"derivedFrom":[subQ1,subQ0]});Q7=makeQuery(id+"F4.imprint","IMPRINT",FACE,{"disambiguationData":[TD([[makeQuery(id+"F4.imprint","IMPRINT",EDGE,{"disambiguationData":[TD([[subQ2,-1.0]])],"derivedFrom":subQ1}),1.0]])]});}
            var Q8;
            {var subQ0=sQuery(id+"F4.wireOp",EDGE,"E34.right");var subQ1=sQuery(id+"F4.wireOp",EDGE,"E24");var subQ2=makeQuery(id+"F4.imprint","INTERSECT",VERTEX,{"derivedFrom":[subQ1,subQ0]});Q8=makeQuery(id+"F4.imprint","IMPRINT",FACE,{"disambiguationData":[TD([[makeQuery(id+"F4.imprint","IMPRINT",EDGE,{"disambiguationData":[TD([[subQ2,-1.0]])],"derivedFrom":subQ1}),1.0]])]});}
            var Q9;
            {var subQ0=sQuery(id+"F4.wireOp",EDGE,"E36");var subQ1=sQuery(id+"F4.wireOp",EDGE,"E23");var subQ2=makeQuery(id+"F4.imprint","INTERSECT",VERTEX,{"disambiguationData":[OD(0.0)],"derivedFrom":[subQ1,subQ0]});Q9=makeQuery(id+"F4.imprint","IMPRINT",FACE,{"disambiguationData":[TD([[makeQuery(id+"F4.imprint","IMPRINT",EDGE,{"disambiguationData":[TD([[subQ2,-1.0]])],"derivedFrom":subQ1}),1.0]])]});}
            var Q10;
            {var subQ0=sQuery(id+"F4.wireOp",EDGE,"E36");var subQ1=sQuery(id+"F4.wireOp",EDGE,"E23");var subQ2=makeQuery(id+"F4.imprint","INTERSECT",VERTEX,{"disambiguationData":[OD(0.0)],"derivedFrom":[subQ1,subQ0]});Q10=makeQuery(id+"F4.imprint","IMPRINT",FACE,{"disambiguationData":[TD([[makeQuery(id+"F4.imprint","IMPRINT",EDGE,{"disambiguationData":[TD([[subQ2,-1.0]])],"derivedFrom":subQ1}),-1.0]])]});}
            var Q11;
            {var subQ0=sQuery(id+"F4.wireOp",EDGE,"E38");var subQ1=sQuery(id+"F4.wireOp",EDGE,"E23");var subQ2=makeQuery(id+"F4.imprint","INTERSECT",VERTEX,{"disambiguationData":[OD(0.0)],"derivedFrom":[subQ1,subQ0]});Q11=makeQuery(id+"F4.imprint","IMPRINT",FACE,{"disambiguationData":[TD([[makeQuery(id+"F4.imprint","IMPRINT",EDGE,{"disambiguationData":[TD([[subQ2,-1.0]])],"derivedFrom":subQ1}),-1.0]])]});}
            var Q12;
            {var subQ0=sQuery(id+"F4.wireOp",EDGE,"E38");var subQ1=sQuery(id+"F4.wireOp",EDGE,"E23");var subQ2=makeQuery(id+"F4.imprint","INTERSECT",VERTEX,{"disambiguationData":[OD(0.0)],"derivedFrom":[subQ1,subQ0]});Q12=makeQuery(id+"F4.imprint","IMPRINT",FACE,{"disambiguationData":[TD([[makeQuery(id+"F4.imprint","IMPRINT",EDGE,{"disambiguationData":[TD([[subQ2,-1.0]])],"derivedFrom":subQ1}),1.0]])]});}
            extrude(context, id + "F6", {"entities" : qUnion([Q0, Q1, Q2, Q3, Q4, Q5, Q6, Q7, Q8, Q9, Q10, Q11, Q12]), "operationType" : NewBodyOperationType.ADD, "depth" : 12.5 * mm, "offsetDistance" : 25 * mm});
        }
        {
            var Q0;
            {var subQ0=sQuery(id+"F4.wireOp",EDGE,"E32");var subQ1=sQuery(id+"F4.wireOp",EDGE,"E23");var subQ2=makeQuery(id+"F4.imprint","INTERSECT",VERTEX,{"disambiguationData":[OD(0.0)],"derivedFrom":[subQ1,subQ0]});Q0=makeQuery(id+"F4.imprint","IMPRINT",FACE,{"disambiguationData":[TD([[makeQuery(id+"F4.imprint","IMPRINT",EDGE,{"disambiguationData":[TD([[subQ2,-1.0]])],"derivedFrom":subQ1}),-1.0]])]});}
            var Q1;
            {var subQ0=sQuery(id+"F4.wireOp",EDGE,"E32");var subQ1=sQuery(id+"F4.wireOp",EDGE,"E23");var subQ2=makeQuery(id+"F4.imprint","INTERSECT",VERTEX,{"disambiguationData":[OD(0.0)],"derivedFrom":[subQ1,subQ0]});Q1=makeQuery(id+"F4.imprint","IMPRINT",FACE,{"disambiguationData":[TD([[makeQuery(id+"F4.imprint","IMPRINT",EDGE,{"disambiguationData":[TD([[subQ2,-1.0]])],"derivedFrom":subQ1}),1.0]])]});}
            var Q2;
            {var subQ0=sQuery(id+"F4.wireOp",EDGE,"E40");var subQ1=sQuery(id+"F4.wireOp",EDGE,"E23");var subQ2=makeQuery(id+"F4.imprint","INTERSECT",VERTEX,{"disambiguationData":[OD(0.0)],"derivedFrom":[subQ1,subQ0]});Q2=makeQuery(id+"F4.imprint","IMPRINT",FACE,{"disambiguationData":[TD([[makeQuery(id+"F4.imprint","IMPRINT",EDGE,{"disambiguationData":[TD([[subQ2,-1.0]])],"derivedFrom":subQ1}),-1.0]])]});}
            var Q3;
            {var subQ0=sQuery(id+"F4.wireOp",EDGE,"E40");var subQ1=sQuery(id+"F4.wireOp",EDGE,"E23");var subQ2=makeQuery(id+"F4.imprint","INTERSECT",VERTEX,{"disambiguationData":[OD(0.0)],"derivedFrom":[subQ1,subQ0]});Q3=makeQuery(id+"F4.imprint","IMPRINT",FACE,{"disambiguationData":[TD([[makeQuery(id+"F4.imprint","IMPRINT",EDGE,{"disambiguationData":[TD([[subQ2,-1.0]])],"derivedFrom":subQ1}),1.0]])]});}
            var Q4;
            {var subQ0=sQuery(id+"F4.wireOp",EDGE,"E42");var subQ1=sQuery(id+"F4.wireOp",EDGE,"E23");var subQ2=makeQuery(id+"F4.imprint","INTERSECT",VERTEX,{"disambiguationData":[OD(0.0)],"derivedFrom":[subQ1,subQ0]});Q4=makeQuery(id+"F4.imprint","IMPRINT",FACE,{"disambiguationData":[TD([[makeQuery(id+"F4.imprint","IMPRINT",EDGE,{"disambiguationData":[TD([[subQ2,-1.0]])],"derivedFrom":subQ1}),-1.0]])]});}
            var Q5;
            {var subQ0=sQuery(id+"F4.wireOp",EDGE,"E42");var subQ1=sQuery(id+"F4.wireOp",EDGE,"E23");var subQ2=makeQuery(id+"F4.imprint","INTERSECT",VERTEX,{"disambiguationData":[OD(0.0)],"derivedFrom":[subQ1,subQ0]});Q5=makeQuery(id+"F4.imprint","IMPRINT",FACE,{"disambiguationData":[TD([[makeQuery(id+"F4.imprint","IMPRINT",EDGE,{"disambiguationData":[TD([[subQ2,-1.0]])],"derivedFrom":subQ1}),1.0]])]});}
            var Q6;
            {var subQ0=sQuery(id+"F4.wireOp",EDGE,"E38");var subQ1=sQuery(id+"F4.wireOp",EDGE,"E23");var subQ2=makeQuery(id+"F4.imprint","INTERSECT",VERTEX,{"disambiguationData":[OD(0.0)],"derivedFrom":[subQ1,subQ0]});Q6=makeQuery(id+"F4.imprint","IMPRINT",FACE,{"disambiguationData":[TD([[makeQuery(id+"F4.imprint","IMPRINT",EDGE,{"disambiguationData":[TD([[subQ2,-1.0]])],"derivedFrom":subQ1}),-1.0]])]});}
            var Q7;
            {var subQ0=sQuery(id+"F4.wireOp",EDGE,"E38");var subQ1=sQuery(id+"F4.wireOp",EDGE,"E23");var subQ2=makeQuery(id+"F4.imprint","INTERSECT",VERTEX,{"disambiguationData":[OD(0.0)],"derivedFrom":[subQ1,subQ0]});Q7=makeQuery(id+"F4.imprint","IMPRINT",FACE,{"disambiguationData":[TD([[makeQuery(id+"F4.imprint","IMPRINT",EDGE,{"disambiguationData":[TD([[subQ2,-1.0]])],"derivedFrom":subQ1}),1.0]])]});}
            var Q8;
            {var subQ0=sQuery(id+"F4.wireOp",EDGE,"E36");var subQ1=sQuery(id+"F4.wireOp",EDGE,"E23");var subQ2=makeQuery(id+"F4.imprint","INTERSECT",VERTEX,{"disambiguationData":[OD(0.0)],"derivedFrom":[subQ1,subQ0]});Q8=makeQuery(id+"F4.imprint","IMPRINT",FACE,{"disambiguationData":[TD([[makeQuery(id+"F4.imprint","IMPRINT",EDGE,{"disambiguationData":[TD([[subQ2,-1.0]])],"derivedFrom":subQ1}),1.0]])]});}
            var Q9;
            {var subQ0=sQuery(id+"F4.wireOp",EDGE,"E36");var subQ1=sQuery(id+"F4.wireOp",EDGE,"E23");var subQ2=makeQuery(id+"F4.imprint","INTERSECT",VERTEX,{"disambiguationData":[OD(0.0)],"derivedFrom":[subQ1,subQ0]});Q9=makeQuery(id+"F4.imprint","IMPRINT",FACE,{"disambiguationData":[TD([[makeQuery(id+"F4.imprint","IMPRINT",EDGE,{"disambiguationData":[TD([[subQ2,-1.0]])],"derivedFrom":subQ1}),-1.0]])]});}
            var Q10;
            {var subQ0=sQuery(id+"F4.wireOp",EDGE,"E34.right");var subQ1=sQuery(id+"F4.wireOp",EDGE,"E24");var subQ2=makeQuery(id+"F4.imprint","INTERSECT",VERTEX,{"derivedFrom":[subQ1,subQ0]});Q10=makeQuery(id+"F4.imprint","IMPRINT",FACE,{"disambiguationData":[TD([[makeQuery(id+"F4.imprint","IMPRINT",EDGE,{"disambiguationData":[TD([[subQ2,-1.0]])],"derivedFrom":subQ1}),1.0]])]});}
            var Q11;
            {var subQ0=sQuery(id+"F4.wireOp",EDGE,"E34.right");var subQ1=sQuery(id+"F4.wireOp",EDGE,"E23");var subQ2=makeQuery(id+"F4.imprint","INTERSECT",VERTEX,{"derivedFrom":[subQ1,subQ0]});Q11=makeQuery(id+"F4.imprint","IMPRINT",FACE,{"disambiguationData":[TD([[makeQuery(id+"F4.imprint","IMPRINT",EDGE,{"disambiguationData":[TD([[subQ2,-1.0]])],"derivedFrom":subQ1}),1.0]])]});}
            var Q12;
            {var subQ4=sQuery(id+"F4.wireOp",EDGE,"E34.bottom");Q12=makeQuery(id+"F4.imprint","IMPRINT",FACE,{"disambiguationData":[TD([[makeQuery(id+"F4.imprint","IMPRINT",EDGE,{"derivedFrom":subQ4}),-1.0]])]});}
            extrude(context, id + "F7", {"entities" : qUnion([Q0, Q1, Q2, Q3, Q4, Q5, Q6, Q7, Q8, Q9, Q10, Q11, Q12]), "operationType" : NewBodyOperationType.REMOVE, "depth" : 3 * mm, "offsetDistance" : 25 * mm});
        }
        {
            var Q0;
            {var subQ0=sQuery(id+"F0.wireOp",EDGE,"E1");Q0=makeQuery(id+"F5.boolean.opBoolean","INTERSECT",EDGE,{"derivedFrom":[makeQuery(id+"F1.opExtrude","SWEPT_FACE",FACE,{"disambiguationData":[OSD([subQ0]),TDD([makeQuery(id+"F0.imprint","IMPRINT",EDGE,{"disambiguationData":[TD([[makeQuery(id+"F0.imprint","INTERSECT",VERTEX,{"derivedFrom":[subQ0,sQuery(id+"F0.wireOp",EDGE,"E8.bottom"),sQuery(id+"F0.wireOp",EDGE,"E8.left")]}),-1.0]])],"derivedFrom":subQ0})])]}),makeQuery(id+"F5.opExtrude","SWEPT_FACE",FACE,{"disambiguationData":[OSD([sQuery(id+"F4.wireOp",EDGE,"E33")])]})]});}
            var Q1;
            {var subQ0=sQuery(id+"F0.wireOp",EDGE,"E1");Q1=makeQuery(id+"F5.boolean.opBoolean","INTERSECT",EDGE,{"derivedFrom":[makeQuery(id+"F1.opExtrude","SWEPT_FACE",FACE,{"disambiguationData":[OSD([subQ0]),TDD([makeQuery(id+"F0.imprint","IMPRINT",EDGE,{"disambiguationData":[TD([[makeQuery(id+"F0.imprint","INTERSECT",VERTEX,{"derivedFrom":[subQ0,sQuery(id+"F0.wireOp",EDGE,"E8.bottom"),sQuery(id+"F0.wireOp",EDGE,"E8.right")]}),1.0]])],"derivedFrom":subQ0})])]}),makeQuery(id+"F5.opExtrude","SWEPT_FACE",FACE,{"disambiguationData":[OSD([sQuery(id+"F4.wireOp",EDGE,"E33")])]})]});}
            var Q2;
            {var subQ0=sQuery(id+"F0.wireOp",EDGE,"E1");Q2=makeQuery(id+"F5.boolean.opBoolean","INTERSECT",EDGE,{"derivedFrom":[makeQuery(id+"F1.opExtrude","SWEPT_FACE",FACE,{"disambiguationData":[OSD([subQ0]),TDD([makeQuery(id+"F0.imprint","IMPRINT",EDGE,{"disambiguationData":[TD([[makeQuery(id+"F0.imprint","INTERSECT",VERTEX,{"derivedFrom":[subQ0,sQuery(id+"F0.wireOp",EDGE,"E17.bottom"),sQuery(id+"F0.wireOp",EDGE,"E17.right")]}),1.0]])],"derivedFrom":subQ0})])]}),makeQuery(id+"F5.opExtrude","SWEPT_FACE",FACE,{"disambiguationData":[OSD([sQuery(id+"F4.wireOp",EDGE,"E41")])]})]});}
            var Q3;
            {var subQ0=sQuery(id+"F0.wireOp",EDGE,"E1");Q3=makeQuery(id+"F5.boolean.opBoolean","INTERSECT",EDGE,{"derivedFrom":[makeQuery(id+"F1.opExtrude","SWEPT_FACE",FACE,{"disambiguationData":[OSD([subQ0]),TDD([makeQuery(id+"F0.imprint","IMPRINT",EDGE,{"disambiguationData":[TD([[makeQuery(id+"F0.imprint","INTERSECT",VERTEX,{"derivedFrom":[subQ0,sQuery(id+"F0.wireOp",EDGE,"E13.bottom"),sQuery(id+"F0.wireOp",EDGE,"E13.right")]}),1.0]])],"derivedFrom":subQ0})])]}),makeQuery(id+"F5.opExtrude","SWEPT_FACE",FACE,{"disambiguationData":[OSD([sQuery(id+"F4.wireOp",EDGE,"E39")])]})]});}
            var Q4;
            {var subQ0=sQuery(id+"F0.wireOp",EDGE,"E1");Q4=makeQuery(id+"F5.boolean.opBoolean","INTERSECT",EDGE,{"derivedFrom":[makeQuery(id+"F1.opExtrude","SWEPT_FACE",FACE,{"disambiguationData":[OSD([subQ0]),TDD([makeQuery(id+"F0.imprint","IMPRINT",EDGE,{"disambiguationData":[TD([[makeQuery(id+"F0.imprint","INTERSECT",VERTEX,{"derivedFrom":[subQ0,sQuery(id+"F0.wireOp",EDGE,"E12.top"),sQuery(id+"F0.wireOp",EDGE,"E12.left")]}),1.0]])],"derivedFrom":subQ0})])]}),makeQuery(id+"F5.opExtrude","SWEPT_FACE",FACE,{"disambiguationData":[OSD([sQuery(id+"F4.wireOp",EDGE,"E39")])]})]});}
            var Q5;
            {var subQ0=sQuery(id+"F0.wireOp",EDGE,"E1");Q5=makeQuery(id+"F5.boolean.opBoolean","INTERSECT",EDGE,{"derivedFrom":[makeQuery(id+"F1.opExtrude","SWEPT_FACE",FACE,{"disambiguationData":[OSD([subQ0]),TDD([makeQuery(id+"F0.imprint","IMPRINT",EDGE,{"disambiguationData":[TD([[makeQuery(id+"F0.imprint","INTERSECT",VERTEX,{"derivedFrom":[subQ0,sQuery(id+"F0.wireOp",EDGE,"E18.bottom"),sQuery(id+"F0.wireOp",EDGE,"E18.right")]}),1.0]])],"derivedFrom":subQ0})])]}),makeQuery(id+"F5.opExtrude","SWEPT_FACE",FACE,{"disambiguationData":[OSD([sQuery(id+"F4.wireOp",EDGE,"E41")])]})]});}
            var Q6;
            {var subQ0=sQuery(id+"F0.wireOp",EDGE,"E1");Q6=makeQuery(id+"F5.boolean.opBoolean","INTERSECT",EDGE,{"derivedFrom":[makeQuery(id+"F1.opExtrude","SWEPT_FACE",FACE,{"disambiguationData":[OSD([subQ0]),TDD([makeQuery(id+"F0.imprint","IMPRINT",EDGE,{"disambiguationData":[TD([[makeQuery(id+"F0.imprint","INTERSECT",VERTEX,{"derivedFrom":[subQ0,sQuery(id+"F0.wireOp",EDGE,"E8.top"),sQuery(id+"F0.wireOp",EDGE,"E8.left")]}),1.0]])],"derivedFrom":subQ0})])]}),makeQuery(id+"F5.opExtrude","SWEPT_FACE",FACE,{"disambiguationData":[OSD([sQuery(id+"F4.wireOp",EDGE,"E31")])]})]});}
            var Q7;
            {var subQ0=sQuery(id+"F0.wireOp",EDGE,"E1");Q7=makeQuery(id+"F5.boolean.opBoolean","INTERSECT",EDGE,{"derivedFrom":[makeQuery(id+"F1.opExtrude","SWEPT_FACE",FACE,{"disambiguationData":[OSD([subQ0]),TDD([makeQuery(id+"F0.imprint","IMPRINT",EDGE,{"disambiguationData":[TD([[makeQuery(id+"F0.imprint","INTERSECT",VERTEX,{"derivedFrom":[subQ0,sQuery(id+"F0.wireOp",EDGE,"E8.top"),sQuery(id+"F0.wireOp",EDGE,"E8.right")]}),-1.0]])],"derivedFrom":subQ0})])]}),makeQuery(id+"F5.opExtrude","SWEPT_FACE",FACE,{"disambiguationData":[OSD([sQuery(id+"F4.wireOp",EDGE,"E31")])]})]});}
            var Q8;
            {var subQ0=sQuery(id+"F0.wireOp",EDGE,"E1");Q8=makeQuery(id+"F5.boolean.opBoolean","INTERSECT",EDGE,{"derivedFrom":[makeQuery(id+"F1.opExtrude","SWEPT_FACE",FACE,{"disambiguationData":[OSD([subQ0]),TDD([makeQuery(id+"F0.imprint","IMPRINT",EDGE,{"disambiguationData":[TD([[makeQuery(id+"F0.imprint","INTERSECT",VERTEX,{"derivedFrom":[subQ0,sQuery(id+"F0.wireOp",EDGE,"E18.top"),sQuery(id+"F0.wireOp",EDGE,"E18.left")]}),1.0]])],"derivedFrom":subQ0})])]}),makeQuery(id+"F5.opExtrude","SWEPT_FACE",FACE,{"disambiguationData":[OSD([sQuery(id+"F4.wireOp",EDGE,"E37")])]})]});}
            var Q9;
            {var subQ0=sQuery(id+"F0.wireOp",EDGE,"E1");Q9=makeQuery(id+"F5.boolean.opBoolean","INTERSECT",EDGE,{"derivedFrom":[makeQuery(id+"F1.opExtrude","SWEPT_FACE",FACE,{"disambiguationData":[OSD([subQ0]),TDD([makeQuery(id+"F0.imprint","IMPRINT",EDGE,{"disambiguationData":[TD([[makeQuery(id+"F0.imprint","INTERSECT",VERTEX,{"derivedFrom":[subQ0,sQuery(id+"F0.wireOp",EDGE,"E17.top"),sQuery(id+"F0.wireOp",EDGE,"E17.left")]}),1.0]])],"derivedFrom":subQ0})])]}),makeQuery(id+"F5.opExtrude","SWEPT_FACE",FACE,{"disambiguationData":[OSD([sQuery(id+"F4.wireOp",EDGE,"E37")])]})]});}
            var Q10;
            {var subQ0=sQuery(id+"F0.wireOp",EDGE,"E1");Q10=makeQuery(id+"F5.boolean.opBoolean","INTERSECT",EDGE,{"derivedFrom":[makeQuery(id+"F1.opExtrude","SWEPT_FACE",FACE,{"disambiguationData":[OSD([subQ0]),TDD([makeQuery(id+"F0.imprint","IMPRINT",EDGE,{"disambiguationData":[TD([[makeQuery(id+"F0.imprint","INTERSECT",VERTEX,{"derivedFrom":[subQ0,sQuery(id+"F0.wireOp",EDGE,"E13.top"),sQuery(id+"F0.wireOp",EDGE,"E13.left")]}),1.0]])],"derivedFrom":subQ0})])]}),makeQuery(id+"F5.opExtrude","SWEPT_FACE",FACE,{"disambiguationData":[OSD([sQuery(id+"F4.wireOp",EDGE,"E35")])]})]});}
            var Q11;
            {var subQ0=sQuery(id+"F0.wireOp",EDGE,"E1");Q11=makeQuery(id+"F5.boolean.opBoolean","INTERSECT",EDGE,{"derivedFrom":[makeQuery(id+"F1.opExtrude","SWEPT_FACE",FACE,{"disambiguationData":[OSD([subQ0]),TDD([makeQuery(id+"F0.imprint","IMPRINT",EDGE,{"disambiguationData":[TD([[makeQuery(id+"F0.imprint","INTERSECT",VERTEX,{"derivedFrom":[subQ0,sQuery(id+"F0.wireOp",EDGE,"E12.bottom"),sQuery(id+"F0.wireOp",EDGE,"E12.right")]}),1.0]])],"derivedFrom":subQ0})])]}),makeQuery(id+"F5.opExtrude","SWEPT_FACE",FACE,{"disambiguationData":[OSD([sQuery(id+"F4.wireOp",EDGE,"E35")])]})]});}
            fillet(context, id + "F8", {"entities" : qUnion([Q0, Q1, Q2, Q3, Q4, Q5, Q6, Q7, Q8, Q9, Q10, Q11]), "radius" : 5 * mm, "tangentPropagation" : true, "allowEdgeOverflow" : false});
        }
        {
            var Q0;
            {var subQ0=sQuery(id+"F4.wireOp",EDGE,"E37");var subQ1=sQuery(id+"F4.wireOp",EDGE,"E23");var subQ2=makeQuery(id+"F4.imprint","INTERSECT",VERTEX,{"disambiguationData":[OD(0.0)],"derivedFrom":[subQ1,subQ0]});Q0=makeQuery(id+"F4.imprint","IMPRINT",FACE,{"disambiguationData":[TD([[makeQuery(id+"F4.imprint","IMPRINT",EDGE,{"disambiguationData":[TD([[subQ2,-1.0]])],"derivedFrom":subQ1}),-1.0]])]});}
            var Q1;
            {var subQ0=sQuery(id+"F4.wireOp",EDGE,"E31");var subQ1=sQuery(id+"F4.wireOp",EDGE,"E23");var subQ2=makeQuery(id+"F4.imprint","INTERSECT",VERTEX,{"disambiguationData":[OD(1.0)],"derivedFrom":[subQ1,subQ0]});Q1=makeQuery(id+"F4.imprint","IMPRINT",FACE,{"disambiguationData":[TD([[makeQuery(id+"F4.imprint","IMPRINT",EDGE,{"disambiguationData":[TD([[subQ2,-1.0]])],"derivedFrom":subQ1}),1.0]])]});}
            var Q2;
            {var subQ0=sQuery(id+"F4.wireOp",EDGE,"E31");var subQ1=sQuery(id+"F4.wireOp",EDGE,"E23");var subQ2=makeQuery(id+"F4.imprint","INTERSECT",VERTEX,{"disambiguationData":[OD(0.0)],"derivedFrom":[subQ1,subQ0]});Q2=makeQuery(id+"F4.imprint","IMPRINT",FACE,{"disambiguationData":[TD([[makeQuery(id+"F4.imprint","IMPRINT",EDGE,{"disambiguationData":[TD([[subQ2,-1.0]])],"derivedFrom":subQ1}),-1.0]])]});}
            var Q3;
            {var subQ0=sQuery(id+"F4.wireOp",EDGE,"E39");var subQ1=sQuery(id+"F4.wireOp",EDGE,"E23");var subQ2=makeQuery(id+"F4.imprint","INTERSECT",VERTEX,{"disambiguationData":[OD(1.0)],"derivedFrom":[subQ1,subQ0]});Q3=makeQuery(id+"F4.imprint","IMPRINT",FACE,{"disambiguationData":[TD([[makeQuery(id+"F4.imprint","IMPRINT",EDGE,{"disambiguationData":[TD([[subQ2,-1.0]])],"derivedFrom":subQ1}),1.0]])]});}
            var Q4;
            {var subQ0=sQuery(id+"F4.wireOp",EDGE,"E37");var subQ1=sQuery(id+"F4.wireOp",EDGE,"E23");var subQ2=makeQuery(id+"F4.imprint","INTERSECT",VERTEX,{"disambiguationData":[OD(0.0)],"derivedFrom":[subQ1,subQ0]});Q4=makeQuery(id+"F4.imprint","IMPRINT",FACE,{"disambiguationData":[TD([[makeQuery(id+"F4.imprint","IMPRINT",EDGE,{"disambiguationData":[TD([[subQ2,-1.0]])],"derivedFrom":subQ1}),1.0]])]});}
            var Q5;
            {var subQ0=sQuery(id+"F4.wireOp",EDGE,"E37");var subQ1=sQuery(id+"F4.wireOp",EDGE,"E23");var subQ2=makeQuery(id+"F4.imprint","INTERSECT",VERTEX,{"disambiguationData":[OD(1.0)],"derivedFrom":[subQ1,subQ0]});Q5=makeQuery(id+"F4.imprint","IMPRINT",FACE,{"disambiguationData":[TD([[makeQuery(id+"F4.imprint","IMPRINT",EDGE,{"disambiguationData":[TD([[subQ2,1.0]])],"derivedFrom":subQ1}),1.0]])]});}
            var Q6;
            {var subQ0=sQuery(id+"F4.wireOp",EDGE,"E37");var subQ1=sQuery(id+"F4.wireOp",EDGE,"E24");var subQ2=makeQuery(id+"F4.imprint","INTERSECT",VERTEX,{"disambiguationData":[OD(0.0)],"derivedFrom":[subQ1,subQ0]});Q6=makeQuery(id+"F4.imprint","IMPRINT",FACE,{"disambiguationData":[TD([[makeQuery(id+"F4.imprint","IMPRINT",EDGE,{"disambiguationData":[TD([[subQ2,-1.0]])],"derivedFrom":subQ1}),1.0]])]});}
            var Q7;
            {var subQ0=sQuery(id+"F4.wireOp",EDGE,"E31");var subQ1=sQuery(id+"F4.wireOp",EDGE,"E23");var subQ2=makeQuery(id+"F4.imprint","INTERSECT",VERTEX,{"disambiguationData":[OD(0.0)],"derivedFrom":[subQ1,subQ0]});Q7=makeQuery(id+"F4.imprint","IMPRINT",FACE,{"disambiguationData":[TD([[makeQuery(id+"F4.imprint","IMPRINT",EDGE,{"disambiguationData":[TD([[subQ2,-1.0]])],"derivedFrom":subQ1}),1.0]])]});}
            var Q8;
            {var subQ0=sQuery(id+"F4.wireOp",EDGE,"E31");var subQ1=sQuery(id+"F4.wireOp",EDGE,"E23");var subQ2=makeQuery(id+"F4.imprint","INTERSECT",VERTEX,{"disambiguationData":[OD(1.0)],"derivedFrom":[subQ1,subQ0]});Q8=makeQuery(id+"F4.imprint","IMPRINT",FACE,{"disambiguationData":[TD([[makeQuery(id+"F4.imprint","IMPRINT",EDGE,{"disambiguationData":[TD([[subQ2,1.0]])],"derivedFrom":subQ1}),1.0]])]});}
            var Q9;
            {var subQ0=sQuery(id+"F4.wireOp",EDGE,"E31");var subQ1=sQuery(id+"F4.wireOp",EDGE,"E24");var subQ2=makeQuery(id+"F4.imprint","INTERSECT",VERTEX,{"disambiguationData":[OD(0.0)],"derivedFrom":[subQ1,subQ0]});Q9=makeQuery(id+"F4.imprint","IMPRINT",FACE,{"disambiguationData":[TD([[makeQuery(id+"F4.imprint","IMPRINT",EDGE,{"disambiguationData":[TD([[subQ2,-1.0]])],"derivedFrom":subQ1}),1.0]])]});}
            var Q10;
            {var subQ0=sQuery(id+"F4.wireOp",EDGE,"E24");var subQ1=makeQuery(id+"F4.imprint","INTERSECT",VERTEX,{"derivedFrom":[subQ0,sQuery(id+"F4.wireOp",EDGE,"E40")]});Q10=makeQuery(id+"F4.imprint","IMPRINT",FACE,{"disambiguationData":[TD([[makeQuery(id+"F4.imprint","IMPRINT",EDGE,{"disambiguationData":[TD([[subQ1,1.0]])],"derivedFrom":subQ0}),1.0]])]});}
            var Q11;
            {var subQ0=sQuery(id+"F4.wireOp",EDGE,"E39");var subQ1=sQuery(id+"F4.wireOp",EDGE,"E23");var subQ2=makeQuery(id+"F4.imprint","INTERSECT",VERTEX,{"disambiguationData":[OD(1.0)],"derivedFrom":[subQ1,subQ0]});Q11=makeQuery(id+"F4.imprint","IMPRINT",FACE,{"disambiguationData":[TD([[makeQuery(id+"F4.imprint","IMPRINT",EDGE,{"disambiguationData":[TD([[subQ2,1.0]])],"derivedFrom":subQ1}),1.0]])]});}
            var Q12;
            {var subQ0=sQuery(id+"F4.wireOp",EDGE,"E39");var subQ1=sQuery(id+"F4.wireOp",EDGE,"E23");var subQ2=makeQuery(id+"F4.imprint","INTERSECT",VERTEX,{"disambiguationData":[OD(0.0)],"derivedFrom":[subQ1,subQ0]});Q12=makeQuery(id+"F4.imprint","IMPRINT",FACE,{"disambiguationData":[TD([[makeQuery(id+"F4.imprint","IMPRINT",EDGE,{"disambiguationData":[TD([[subQ2,-1.0]])],"derivedFrom":subQ1}),1.0]])]});}
            var Q13;
            {var subQ0=sQuery(id+"F4.wireOp",EDGE,"E39");var subQ1=sQuery(id+"F4.wireOp",EDGE,"E23");var subQ2=makeQuery(id+"F4.imprint","INTERSECT",VERTEX,{"disambiguationData":[OD(0.0)],"derivedFrom":[subQ1,subQ0]});Q13=makeQuery(id+"F4.imprint","IMPRINT",FACE,{"disambiguationData":[TD([[makeQuery(id+"F4.imprint","IMPRINT",EDGE,{"disambiguationData":[TD([[subQ2,-1.0]])],"derivedFrom":subQ1}),-1.0]])]});}
            var Q14;
            {var subQ0=sQuery(id+"F4.wireOp",EDGE,"E39");var subQ1=sQuery(id+"F4.wireOp",EDGE,"E23");var subQ2=makeQuery(id+"F4.imprint","INTERSECT",VERTEX,{"disambiguationData":[OD(0.0)],"derivedFrom":[subQ1,subQ0]});Q14=makeQuery(id+"F4.imprint","IMPRINT",FACE,{"disambiguationData":[TD([[makeQuery(id+"F4.imprint","IMPRINT",EDGE,{"disambiguationData":[TD([[subQ2,1.0]])],"derivedFrom":subQ1}),1.0]])]});}
            var Q15;
            {var subQ0=sQuery(id+"F4.wireOp",EDGE,"E41");var subQ1=sQuery(id+"F4.wireOp",EDGE,"E23");var subQ2=makeQuery(id+"F4.imprint","INTERSECT",VERTEX,{"disambiguationData":[OD(1.0)],"derivedFrom":[subQ1,subQ0]});Q15=makeQuery(id+"F4.imprint","IMPRINT",FACE,{"disambiguationData":[TD([[makeQuery(id+"F4.imprint","IMPRINT",EDGE,{"disambiguationData":[TD([[subQ2,1.0]])],"derivedFrom":subQ1}),1.0]])]});}
            var Q16;
            {var subQ0=sQuery(id+"F4.wireOp",EDGE,"E41");var subQ1=sQuery(id+"F4.wireOp",EDGE,"E23");var subQ2=makeQuery(id+"F4.imprint","INTERSECT",VERTEX,{"disambiguationData":[OD(0.0)],"derivedFrom":[subQ1,subQ0]});Q16=makeQuery(id+"F4.imprint","IMPRINT",FACE,{"disambiguationData":[TD([[makeQuery(id+"F4.imprint","IMPRINT",EDGE,{"disambiguationData":[TD([[subQ2,-1.0]])],"derivedFrom":subQ1}),1.0]])]});}
            var Q17;
            {var subQ0=sQuery(id+"F4.wireOp",EDGE,"E41");var subQ1=sQuery(id+"F4.wireOp",EDGE,"E24");var subQ2=makeQuery(id+"F4.imprint","INTERSECT",VERTEX,{"disambiguationData":[OD(0.0)],"derivedFrom":[subQ1,subQ0]});Q17=makeQuery(id+"F4.imprint","IMPRINT",FACE,{"disambiguationData":[TD([[makeQuery(id+"F4.imprint","IMPRINT",EDGE,{"disambiguationData":[TD([[subQ2,-1.0]])],"derivedFrom":subQ1}),1.0]])]});}
            var Q18;
            {var subQ0=sQuery(id+"F4.wireOp",EDGE,"E41");var subQ1=sQuery(id+"F4.wireOp",EDGE,"E23");var subQ2=makeQuery(id+"F4.imprint","INTERSECT",VERTEX,{"disambiguationData":[OD(0.0)],"derivedFrom":[subQ1,subQ0]});Q18=makeQuery(id+"F4.imprint","IMPRINT",FACE,{"disambiguationData":[TD([[makeQuery(id+"F4.imprint","IMPRINT",EDGE,{"disambiguationData":[TD([[subQ2,-1.0]])],"derivedFrom":subQ1}),-1.0]])]});}
            var Q19;
            {var subQ0=sQuery(id+"F4.wireOp",EDGE,"E33");var subQ1=sQuery(id+"F4.wireOp",EDGE,"E23");var subQ2=makeQuery(id+"F4.imprint","INTERSECT",VERTEX,{"disambiguationData":[OD(1.0)],"derivedFrom":[subQ1,subQ0]});Q19=makeQuery(id+"F4.imprint","IMPRINT",FACE,{"disambiguationData":[TD([[makeQuery(id+"F4.imprint","IMPRINT",EDGE,{"disambiguationData":[TD([[subQ2,-1.0]])],"derivedFrom":subQ1}),1.0]])]});}
            var Q20;
            {var subQ0=sQuery(id+"F4.wireOp",EDGE,"E34.bottom");Q20=makeQuery(id+"F4.imprint","IMPRINT",FACE,{"disambiguationData":[TD([[makeQuery(id+"F4.imprint","IMPRINT",EDGE,{"derivedFrom":subQ0}),1.0]])]});}
            var Q21;
            {var subQ3=sQuery(id+"F4.wireOp",EDGE,"E24");var subQ5=sQuery(id+"F4.wireOp",EDGE,"E33");var subQ7=makeQuery(id+"F4.imprint","INTERSECT",VERTEX,{"disambiguationData":[OD(0.0)],"derivedFrom":[subQ3,subQ5]});Q21=makeQuery(id+"F4.imprint","IMPRINT",FACE,{"disambiguationData":[TD([[makeQuery(id+"F4.imprint","IMPRINT",EDGE,{"disambiguationData":[TD([[subQ7,-1.0]])],"derivedFrom":subQ3}),1.0]])]});}
            var Q22;
            {var subQ0=sQuery(id+"F4.wireOp",EDGE,"E35");var subQ1=sQuery(id+"F4.wireOp",EDGE,"E23");var subQ2=makeQuery(id+"F4.imprint","INTERSECT",VERTEX,{"disambiguationData":[OD(1.0)],"derivedFrom":[subQ1,subQ0]});Q22=makeQuery(id+"F4.imprint","IMPRINT",FACE,{"disambiguationData":[TD([[makeQuery(id+"F4.imprint","IMPRINT",EDGE,{"disambiguationData":[TD([[subQ2,-1.0]])],"derivedFrom":subQ1}),1.0]])]});}
            var Q23;
            {var subQ0=sQuery(id+"F4.wireOp",EDGE,"E37");var subQ1=sQuery(id+"F4.wireOp",EDGE,"E23");var subQ2=makeQuery(id+"F4.imprint","INTERSECT",VERTEX,{"disambiguationData":[OD(1.0)],"derivedFrom":[subQ1,subQ0]});Q23=makeQuery(id+"F4.imprint","IMPRINT",FACE,{"disambiguationData":[TD([[makeQuery(id+"F4.imprint","IMPRINT",EDGE,{"disambiguationData":[TD([[subQ2,-1.0]])],"derivedFrom":subQ1}),1.0]])]});}
            var Q24;
            {var subQ0=sQuery(id+"F4.wireOp",EDGE,"E35");var subQ1=sQuery(id+"F4.wireOp",EDGE,"E23");var subQ2=makeQuery(id+"F4.imprint","INTERSECT",VERTEX,{"disambiguationData":[OD(0.0)],"derivedFrom":[subQ1,subQ0]});Q24=makeQuery(id+"F4.imprint","IMPRINT",FACE,{"disambiguationData":[TD([[makeQuery(id+"F4.imprint","IMPRINT",EDGE,{"disambiguationData":[TD([[subQ2,-1.0]])],"derivedFrom":subQ1}),-1.0]])]});}
            var Q25;
            {var subQ0=sQuery(id+"F4.wireOp",EDGE,"E35");var subQ1=sQuery(id+"F4.wireOp",EDGE,"E24");var subQ2=makeQuery(id+"F4.imprint","INTERSECT",VERTEX,{"disambiguationData":[OD(0.0)],"derivedFrom":[subQ1,subQ0]});Q25=makeQuery(id+"F4.imprint","IMPRINT",FACE,{"disambiguationData":[TD([[makeQuery(id+"F4.imprint","IMPRINT",EDGE,{"disambiguationData":[TD([[subQ2,-1.0]])],"derivedFrom":subQ1}),1.0]])]});}
            var Q26;
            {var subQ0=sQuery(id+"F4.wireOp",EDGE,"E33");var subQ1=sQuery(id+"F4.wireOp",EDGE,"E23");var subQ2=makeQuery(id+"F4.imprint","INTERSECT",VERTEX,{"disambiguationData":[OD(1.0)],"derivedFrom":[subQ1,subQ0]});Q26=makeQuery(id+"F4.imprint","IMPRINT",FACE,{"disambiguationData":[TD([[makeQuery(id+"F4.imprint","IMPRINT",EDGE,{"disambiguationData":[TD([[subQ2,1.0]])],"derivedFrom":subQ1}),1.0]])]});}
            var Q27;
            {var subQ0=sQuery(id+"F4.wireOp",EDGE,"E33");var subQ1=sQuery(id+"F4.wireOp",EDGE,"E23");var subQ2=makeQuery(id+"F4.imprint","INTERSECT",VERTEX,{"disambiguationData":[OD(0.0)],"derivedFrom":[subQ1,subQ0]});Q27=makeQuery(id+"F4.imprint","IMPRINT",FACE,{"disambiguationData":[TD([[makeQuery(id+"F4.imprint","IMPRINT",EDGE,{"disambiguationData":[TD([[subQ2,-1.0]])],"derivedFrom":subQ1}),1.0]])]});}
            var Q28;
            {var subQ0=sQuery(id+"F4.wireOp",EDGE,"E35");var subQ1=sQuery(id+"F4.wireOp",EDGE,"E23");var subQ2=makeQuery(id+"F4.imprint","INTERSECT",VERTEX,{"disambiguationData":[OD(0.0)],"derivedFrom":[subQ1,subQ0]});Q28=makeQuery(id+"F4.imprint","IMPRINT",FACE,{"disambiguationData":[TD([[makeQuery(id+"F4.imprint","IMPRINT",EDGE,{"disambiguationData":[TD([[subQ2,-1.0]])],"derivedFrom":subQ1}),1.0]])]});}
            var Q29;
            {var subQ0=sQuery(id+"F4.wireOp",EDGE,"E35");var subQ1=sQuery(id+"F4.wireOp",EDGE,"E23");var subQ2=makeQuery(id+"F4.imprint","INTERSECT",VERTEX,{"disambiguationData":[OD(1.0)],"derivedFrom":[subQ1,subQ0]});Q29=makeQuery(id+"F4.imprint","IMPRINT",FACE,{"disambiguationData":[TD([[makeQuery(id+"F4.imprint","IMPRINT",EDGE,{"disambiguationData":[TD([[subQ2,1.0]])],"derivedFrom":subQ1}),1.0]])]});}
            var Q30;
            {var subQ1=sQuery(id+"F4.wireOp",EDGE,"E24");var subQ4=sQuery(id+"F4.wireOp",EDGE,"E39");var subQ14=makeQuery(id+"F4.imprint","INTERSECT",VERTEX,{"disambiguationData":[OD(1.0)],"derivedFrom":[subQ1,subQ4]});Q30=makeQuery(id+"F4.imprint","IMPRINT",FACE,{"disambiguationData":[TD([[makeQuery(id+"F4.imprint","IMPRINT",EDGE,{"disambiguationData":[TD([[subQ14,-1.0]])],"derivedFrom":subQ1}),1.0]])]});}
            extrude(context, id + "F9", {"entities" : qUnion([Q0, Q1, Q2, Q3, Q4, Q5, Q6, Q7, Q8, Q9, Q10, Q11, Q12, Q13, Q14, Q15, Q16, Q17, Q18, Q19, Q20, Q21, Q22, Q23, Q24, Q25, Q26, Q27, Q28, Q29, Q30]), "operationType" : NewBodyOperationType.ADD, "depth" : 1 * mm, "offsetDistance" : 25 * mm});
        }
        {
            var Q0;
            Q0=makeQuery(id+"F7.boolean.opBoolean","COPY",EDGE,{"derivedFrom":makeQuery(id+"F7.opExtrude","CAP_EDGE",EDGE,{"disambiguationData":[OSD([sQuery(id+"F4.wireOp",EDGE,"E32")])],"isStart":false})});
            var Q1;
            Q1=makeQuery(id+"F7.boolean.opBoolean","COPY",EDGE,{"derivedFrom":makeQuery(id+"F7.opExtrude","CAP_EDGE",EDGE,{"disambiguationData":[OSD([sQuery(id+"F4.wireOp",EDGE,"E38")])],"isStart":false})});
            var Q2;
            Q2=makeQuery(id+"F7.boolean.opBoolean","COPY",EDGE,{"derivedFrom":makeQuery(id+"F7.opExtrude","CAP_EDGE",EDGE,{"disambiguationData":[OSD([sQuery(id+"F4.wireOp",EDGE,"E40")])],"isStart":false})});
            var Q3;
            Q3=makeQuery(id+"F7.boolean.opBoolean","COPY",EDGE,{"derivedFrom":makeQuery(id+"F7.opExtrude","CAP_EDGE",EDGE,{"disambiguationData":[OSD([sQuery(id+"F4.wireOp",EDGE,"E42")])],"isStart":false})});
            var Q4;
            Q4=makeQuery(id+"F7.boolean.opBoolean","COPY",EDGE,{"derivedFrom":makeQuery(id+"F7.opExtrude","CAP_EDGE",EDGE,{"disambiguationData":[OSD([sQuery(id+"F4.wireOp",EDGE,"E36")])],"isStart":false})});
            fillet(context, id + "F10", {"entities" : qUnion([Q0, Q1, Q2, Q3, Q4]), "radius" : 1 * mm, "allowEdgeOverflow" : false});
        }
        {
            var Q0;
            Q0=makeQuery(id+"F6.opExtrude","CAP_EDGE",EDGE,{"disambiguationData":[OSD([sQuery(id+"F4.wireOp",EDGE,"E32")])],"isStart":false});
            var Q1;
            Q1=makeQuery(id+"F6.opExtrude","CAP_FACE",FACE,{"disambiguationData":[OSD([sQuery(id+"F4.wireOp",EDGE,"E42")])],"isStart":false});
            var Q2;
            Q2=makeQuery(id+"F6.opExtrude","CAP_FACE",FACE,{"disambiguationData":[OSD([sQuery(id+"F4.wireOp",EDGE,"E40")])],"isStart":false});
            var Q3;
            Q3=makeQuery(id+"F6.opExtrude","CAP_FACE",FACE,{"disambiguationData":[OSD([sQuery(id+"F4.wireOp",EDGE,"E38")])],"isStart":false});
            var Q4;
            Q4=makeQuery(id+"F6.opExtrude","CAP_FACE",FACE,{"disambiguationData":[OSD([sQuery(id+"F4.wireOp",EDGE,"E36")])],"isStart":false});
            fillet(context, id + "F11", {"entities" : qUnion([Q0, Q1, Q2, Q3, Q4]), "radius" : 1 * mm, "tangentPropagation" : true, "allowEdgeOverflow" : false});
        }
        {
            var Q0;
            Q0=makeQuery(id+"F6.opExtrude","CAP_EDGE",EDGE,{"disambiguationData":[OSD([sQuery(id+"F4.wireOp",EDGE,"E34.top")])],"isStart":false});
            var Q1;
            Q1=makeQuery(id+"F6.opExtrude","CAP_EDGE",EDGE,{"disambiguationData":[OSD([sQuery(id+"F4.wireOp",EDGE,"E34.left")])],"isStart":false});
            var Q2;
            Q2=makeQuery(id+"F6.opExtrude","CAP_EDGE",EDGE,{"disambiguationData":[OSD([sQuery(id+"F4.wireOp",EDGE,"E34.bottom")])],"isStart":false});
            var Q3;
            Q3=makeQuery(id+"F6.opExtrude","CAP_EDGE",EDGE,{"disambiguationData":[OSD([sQuery(id+"F4.wireOp",EDGE,"E34.right")])],"isStart":false});
            fillet(context, id + "F12", {"entities" : qUnion([Q0, Q1, Q2, Q3]), "radius" : .8 * mm, "tangentPropagation" : true, "allowEdgeOverflow" : false});
        }
        {
            var Q0;
            Q0=makeQuery(id+"F7.boolean.opBoolean","COPY",EDGE,{"derivedFrom":makeQuery(id+"F7.opExtrude","CAP_EDGE",EDGE,{"disambiguationData":[OSD([sQuery(id+"F4.wireOp",EDGE,"E34.left")])],"isStart":false})});
            var Q1;
            Q1=makeQuery(id+"F7.boolean.opBoolean","COPY",EDGE,{"derivedFrom":makeQuery(id+"F7.opExtrude","CAP_EDGE",EDGE,{"disambiguationData":[OSD([sQuery(id+"F4.wireOp",EDGE,"E34.bottom")])],"isStart":false})});
            var Q2;
            Q2=makeQuery(id+"F7.boolean.opBoolean","COPY",EDGE,{"derivedFrom":makeQuery(id+"F7.opExtrude","CAP_EDGE",EDGE,{"disambiguationData":[OSD([sQuery(id+"F4.wireOp",EDGE,"E34.top")])],"isStart":false})});
            var Q3;
            Q3=makeQuery(id+"F7.boolean.opBoolean","COPY",EDGE,{"derivedFrom":makeQuery(id+"F7.opExtrude","CAP_EDGE",EDGE,{"disambiguationData":[OSD([sQuery(id+"F4.wireOp",EDGE,"E34.right")])],"isStart":false})});
            fillet(context, id + "F13", {"entities" : qUnion([Q0, Q1, Q2, Q3]), "radius" : .8 * mm, "tangentPropagation" : true, "allowEdgeOverflow" : false});
        }
    });
